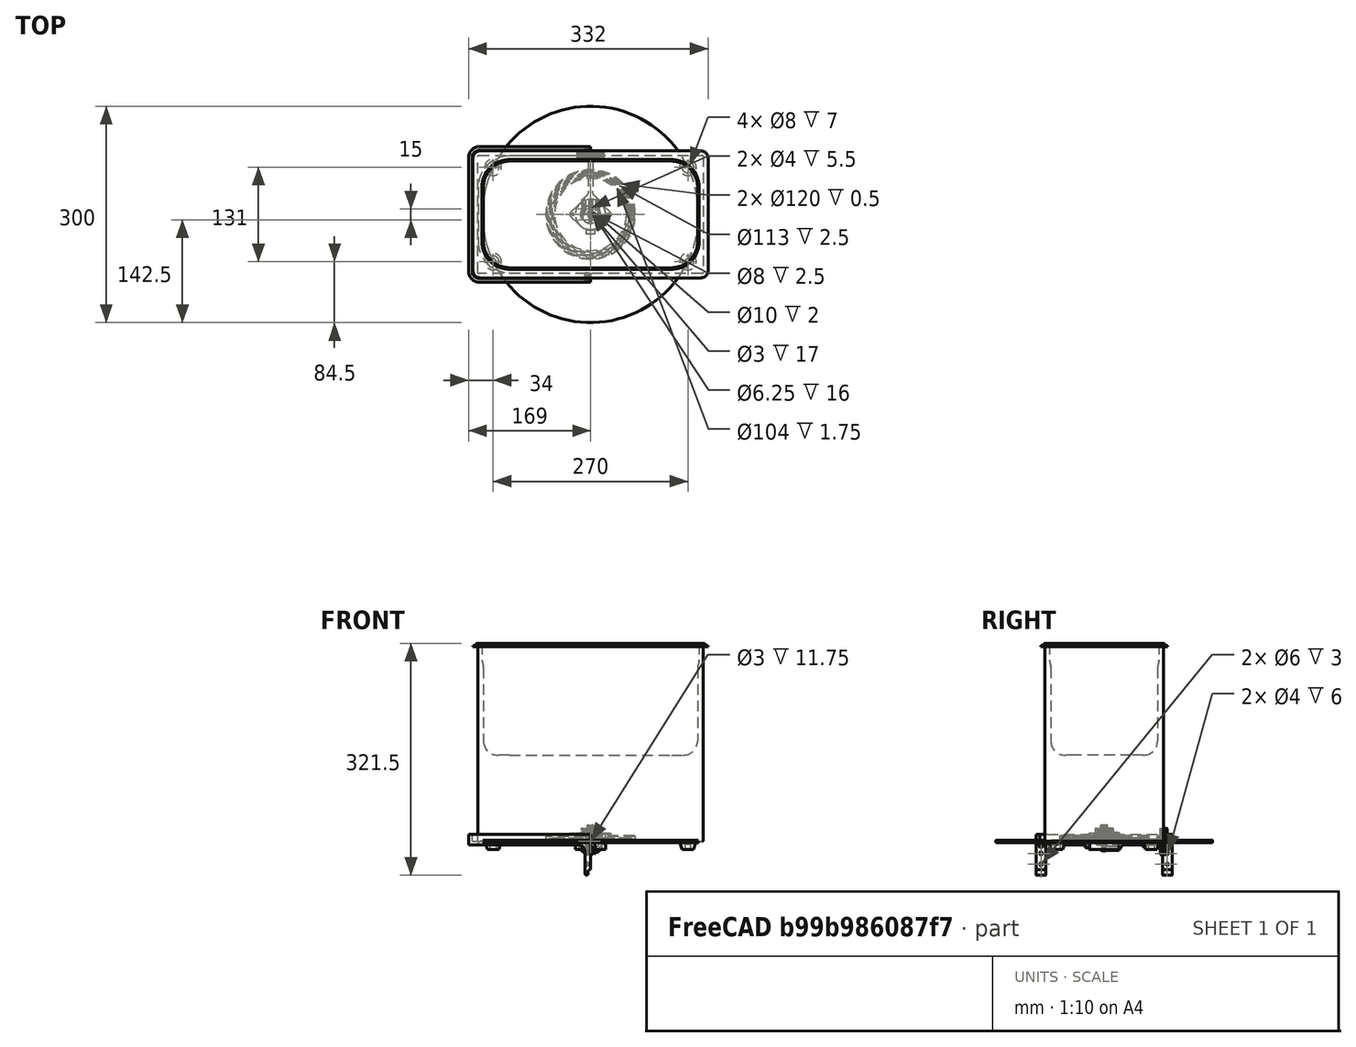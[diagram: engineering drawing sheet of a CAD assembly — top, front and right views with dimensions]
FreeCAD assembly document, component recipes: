
FREECAD ASSEMBLY — COMPONENT RECIPES ("assembly-ultrasonic-cleaner-exploded")

This assembly document has 14 components, labeled P0..P13 below (a component is one placed body or linked part). 14 of them carry a construction recipe — the FreeCAD feature program that regenerates the part from scratch, quoted from this document or its linked companion documents; the rest are supplied as boundary geometry only. No exploded tour is included for this assembly.
NOTE — this tour is split across 2 documents so each fits a 32k-token context. This is document 1: the component sections continue in the remaining 1 document, each repeating the header above.
COMPONENT P0 — recipe-attached ("Body", modeled in this document).
Construction recipe (the document's own serialized feature program — sketch geometry with constraints, then the solid features built on it; lengths are millimeters unless a unit is written):

FEATURE [Sketcher::SketchObject] CopySketch004
  ArcFitTolerance = 0
  ExternalBSplineMaxDegree = 0
  ExternalBSplineTolerance = 0
  FullyConstrained = false
  InternalTolerance = 1e-06
  InvalidShape = false
  MakeInternals = false
  Placement = pos=(0,0,250.5) rot=(0,0,1;0rad)
  TreeRank = 0
  ValidateShape = false
  sketch-geometry (8):
    g0: ArcOfCircle CenterX=112.315 CenterY=-37.8146 CenterZ=0 NormalX=0 NormalY=0 NormalZ=1 AngleXU=0 Radius=38.1854 StartAngle=4.71239 EndAngle=6.28319
    g1: ArcOfCircle CenterX=112.315 CenterY=37.8146 CenterZ=0 NormalX=0 NormalY=0 NormalZ=1 AngleXU=0 Radius=38.1854 StartAngle=2e-16 EndAngle=1.5708
    g2: ArcOfCircle CenterX=-112.315 CenterY=37.8146 CenterZ=0 NormalX=0 NormalY=0 NormalZ=1 AngleXU=0 Radius=38.1854 StartAngle=1.5708 EndAngle=3.14159
    g3: ArcOfCircle CenterX=-112.315 CenterY=-37.8146 CenterZ=0 NormalX=0 NormalY=0 NormalZ=1 AngleXU=0 Radius=38.1854 StartAngle=3.14159 EndAngle=4.71239
    g4: LineSegment StartX=150.5 StartY=-37.8146 StartZ=0 EndX=150.5 EndY=37.8146 EndZ=0
    g5: LineSegment StartX=112.315 StartY=-76 StartZ=0 EndX=-112.315 EndY=-76 EndZ=0
    g6: LineSegment StartX=-150.5 StartY=-37.8146 StartZ=0 EndX=-150.5 EndY=37.8146 EndZ=0
    g7: LineSegment StartX=112.315 StartY=76 StartZ=0 EndX=-112.315 EndY=76 EndZ=0
  constraints (14):
    c: Symmetric(g4,g6,g-2)
    c: Symmetric(g6,g4,g-2)
    c: Symmetric(g4,g4,g-1)
    c: Symmetric(g5,g7,g-1)
    c: Symmetric(g5,g7,g-1)
    c: Symmetric(g5,g5,g-2)
    c: Tangent(g0,g4) = -1.5708
    c: Tangent(g4,g1) = -1.5708
    c: Tangent(g1,g7) = -1.5708
    c: Tangent(g2,g7) = -1.5708
    c: Tangent(g6,g2) = 1.5708
    c: Tangent(g3,g6) = 1.5708
    c: Tangent(g3,g5) = 1.5708
    c: Tangent(g0,g5) = 1.5708
FEATURE [Sketcher::SketchObject] Sketch
  ArcFitTolerance = 0
  AttachmentSupport = -> [XY_Plane]
  ExternalBSplineMaxDegree = 0
  ExternalBSplineTolerance = 0
  FullyConstrained = false
  InternalTolerance = 1e-06
  InvalidShape = false
  MakeInternals = false
  MapMode = 5
  Support = -> [XY_Plane]
  TreeRank = 0
  ValidateShape = false
  sketch-geometry (4):
    g0: LineSegment StartX=-156 StartY=82 StartZ=0 EndX=156 EndY=82 EndZ=0
    g1: LineSegment StartX=156 StartY=82 StartZ=0 EndX=156 EndY=-82 EndZ=0
    g2: LineSegment StartX=156 StartY=-82 StartZ=0 EndX=-156 EndY=-82 EndZ=0
    g3: LineSegment StartX=-156 StartY=-82 StartZ=0 EndX=-156 EndY=82 EndZ=0
  constraints (10):
    c: Coincident(g0,g1)
    c: Coincident(g1,g2)
    c: Coincident(g2,g3)
    c: Coincident(g3,g0)
    c: Horizontal(g2)
    c: Vertical(g1)
    c: Symmetric(g0,g2,g-1)
    c: Symmetric(g0,g0,g-2)
    c: DistanceX(g0,g0) = 312
    c: DistanceY(g3,g3) = 164
FEATURE [PartDesign::Pad] Pad
  AddSubType = 0
  AllowMultiFace = false
  AutoTaperInnerAngle = true
  CheckUpToFaceLimits = true
  ClaimChildren = false
  Direction = (1,1,1)
  Fit = 0
  FitJoin = 0
  InnerFit = 0
  InnerFitJoin = 0
  InvalidShape = false
  Length = 270
  Length2 = 100
  NewSolid = false
  Profile = -> Sketch
  Suppress = false
  TaperInnerAngle = 0
  TaperInnerAngleRev = 0
  TreeRank = 0
  Type = 0
  ValidateShape = true
  _ProfileBasedVersion = 0
FEATURE [Sketcher::SketchObject] Sketch001
  ArcFitTolerance = 0
  AttachmentSupport = -> [Pad]
  ExternalBSplineMaxDegree = 0
  ExternalBSplineTolerance = 0
  FullyConstrained = false
  InternalTolerance = 1e-06
  InvalidShape = false
  MakeInternals = false
  MapMode = 5
  Placement = pos=(0,0,270) rot=(0,0,1;0rad)
  Support = -> [Pad]
  TreeRank = 0
  ValidateShape = false
  sketch-geometry (4):
    g0: LineSegment StartX=-163 StartY=88 StartZ=0 EndX=163 EndY=88 EndZ=0
    g1: LineSegment StartX=163 StartY=88 StartZ=0 EndX=163 EndY=-88 EndZ=0
    g2: LineSegment StartX=163 StartY=-88 StartZ=0 EndX=-163 EndY=-88 EndZ=0
    g3: LineSegment StartX=-163 StartY=-88 StartZ=0 EndX=-163 EndY=88 EndZ=0
  constraints (10):
    c: Coincident(g0,g1)
    c: Coincident(g1,g2)
    c: Coincident(g2,g3)
    c: Coincident(g3,g0)
    c: Horizontal(g2)
    c: Vertical(g1)
    c: DistanceX(g0,g0) = 326
    c: DistanceY(g3,g3) = 176
    c: Symmetric(g0,g2,g-1)
    c: Symmetric(g0,g0,g-2)
FEATURE [PartDesign::Pad] Pad001
  AddSubType = 0
  AllowMultiFace = false
  AutoTaperInnerAngle = true
  BaseFeature = -> Pad
  CheckUpToFaceLimits = true
  ClaimChildren = false
  Direction = (1,1,1)
  Fit = 0
  FitJoin = 0
  InnerFit = 0
  InnerFitJoin = 0
  InvalidShape = false
  Length = 1.5
  Length2 = 100
  NewSolid = false
  Profile = -> Sketch001
  Suppress = false
  TaperInnerAngle = 0
  TaperInnerAngleRev = 0
  TreeRank = 0
  Type = 0
  ValidateShape = true
  _ProfileBasedVersion = 0
FEATURE [PartDesign::Fillet] Fillet
  AddSubType = 0
  Base = -> Pad001 [Edge22,Edge18,Edge17,Edge20]
  BaseFeature = -> Pad001
  InvalidShape = false
  NewSolid = false
  Radius = 10
  SupportTransform = false
  Suppress = false
  TreeRank = 0
  UseAllEdges = false
  ValidateShape = true
FEATURE [Sketcher::SketchObject] Sketch002
  ArcFitTolerance = 0
  AttachmentSupport = -> [Fillet]
  ExternalBSplineMaxDegree = 0
  ExternalBSplineTolerance = 0
  ExternalGeometry = -> [Fillet]
  FullyConstrained = false
  InternalTolerance = 1e-06
  InvalidShape = false
  MakeInternals = false
  MapMode = 5
  Placement = pos=(0,0,271.5) rot=(0,0,1;0rad)
  Support = -> [Fillet]
  TreeRank = 0
  ValidateShape = false
  sketch-geometry (8):
    g0: LineSegment StartX=-158 StartY=78 StartZ=0 EndX=-158 EndY=-78 EndZ=0
    g1: LineSegment StartX=-153 StartY=-83 StartZ=0 EndX=153 EndY=-83 EndZ=0
    g2: LineSegment StartX=158 StartY=-78 StartZ=0 EndX=158 EndY=78 EndZ=0
    g3: LineSegment StartX=153 StartY=83 StartZ=0 EndX=-153 EndY=83 EndZ=0
    g4: ArcOfCircle CenterX=-153 CenterY=78 CenterZ=0 NormalX=0 NormalY=0 NormalZ=1 AngleXU=0 Radius=5 StartAngle=1.5708 EndAngle=3.14159
    g5: ArcOfCircle CenterX=-153 CenterY=-78 CenterZ=0 NormalX=0 NormalY=0 NormalZ=1 AngleXU=0 Radius=5 StartAngle=3.14159 EndAngle=4.71239
    g6: ArcOfCircle CenterX=153 CenterY=-78 CenterZ=0 NormalX=0 NormalY=0 NormalZ=1 AngleXU=0 Radius=5 StartAngle=4.71239 EndAngle=6.28319
    g7: ArcOfCircle CenterX=153 CenterY=78 CenterZ=0 NormalX=0 NormalY=0 NormalZ=1 AngleXU=0 Radius=5 StartAngle=-9e-16 EndAngle=1.5708
  constraints (17):
    c: Vertical(g0)
    c: Horizontal(g1)
    c: Symmetric(g1,g3,g-1)
    c: Symmetric(g3,g1,g-1)
    c: Symmetric(g0,g2,g-2)
    c: Symmetric(g2,g0,g-2)
    c: Tangent(g7,g3) = -1.5708
    c: Tangent(g7,g2) = -1.5708
    c: Tangent(g6,g2) = -1.5708
    c: Tangent(g1,g6) = -1.5708
    c: Tangent(g1,g5) = -1.5708
    c: Tangent(g5,g0) = -1.5708
    c: Tangent(g4,g0) = -1.5708
    c: Tangent(g4,g3) = -1.5708
    c: DistanceY(g3,g-10) = 5
    c: DistanceX(g-4,g0) = 5
    c: Horizontal(g-4,g0)
FEATURE [PartDesign::Pad] Pad002
  AddSubType = 0
  AllowMultiFace = false
  AutoTaperInnerAngle = true
  BaseFeature = -> Fillet
  CheckUpToFaceLimits = true
  ClaimChildren = false
  Direction = (1,1,1)
  Fit = 0
  FitJoin = 0
  InnerFit = 0
  InnerFitJoin = 0
  InvalidShape = false
  Length = 3
  Length2 = 100
  NewSolid = false
  Profile = -> Sketch002
  Suppress = false
  TaperInnerAngle = 0
  TaperInnerAngleRev = 0
  TreeRank = 0
  Type = 0
  ValidateShape = true
  _ProfileBasedVersion = 0
FEATURE [PartDesign::Draft] Draft
  AddSubType = 0
  Angle = 45
  Base = -> Pad002 [Face21,Face22,Face23,Face16,Face17,Face18,Face19,Face20]
  BaseFeature = -> Pad002
  InvalidShape = false
  NeutralPlane = -> Pad002 [Face24]
  NewSolid = false
  SupportTransform = false
  Suppress = false
  TreeRank = 0
  ValidateShape = true
FEATURE [PartDesign::Fillet] Fillet001
  AddSubType = 0
  Base = -> Draft [Edge59,Edge60,Edge44,Edge43,Edge42,Edge57,Edge55,Edge41,Edge53,Edge40,Edge51,Edge49,Edge38,Edge39,Edge47,Edge37]
  BaseFeature = -> Draft
  InvalidShape = false
  NewSolid = false
  Radius = 4
  SupportTransform = false
  Suppress = false
  TreeRank = 0
  UseAllEdges = false
  ValidateShape = true
FEATURE [Sketcher::SketchObject] Sketch003
  ArcFitTolerance = 0
  AttachmentSupport = -> [Fillet001]
  ExternalBSplineMaxDegree = 0
  ExternalBSplineTolerance = 0
  ExternalGeometry = -> [Fillet001]
  FullyConstrained = false
  InternalTolerance = 1e-06
  InvalidShape = false
  MakeInternals = false
  MapMode = 5
  Placement = pos=(0,0,274.5) rot=(0,0,1;0rad)
  Support = -> [Fillet001]
  TreeRank = 0
  ValidateShape = false
  sketch-geometry (9):
    g0: ArcOfCircle CenterX=-112.315 CenterY=37.8146 CenterZ=0 NormalX=0 NormalY=0 NormalZ=1 AngleXU=0 Radius=38.1854 StartAngle=1.5708 EndAngle=3.14159
    g1: ArcOfCircle CenterX=-112.315 CenterY=-37.8146 CenterZ=0 NormalX=0 NormalY=0 NormalZ=1 AngleXU=0 Radius=38.1854 StartAngle=3.14159 EndAngle=4.71239
    g2: ArcOfCircle CenterX=112.315 CenterY=-37.8146 CenterZ=0 NormalX=0 NormalY=0 NormalZ=1 AngleXU=0 Radius=38.1854 StartAngle=4.71239 EndAngle=6.28319
    g3: ArcOfCircle CenterX=112.315 CenterY=37.8146 CenterZ=0 NormalX=0 NormalY=0 NormalZ=1 AngleXU=0 Radius=38.1854 StartAngle=0 EndAngle=1.5708
    g4: LineSegment StartX=-150.5 StartY=37.8146 StartZ=0 EndX=-150.5 EndY=-37.8146 EndZ=0
    g5: LineSegment StartX=-112.315 StartY=76 StartZ=0 EndX=112.315 EndY=76 EndZ=0
    g6: LineSegment StartX=-112.315 StartY=-76 StartZ=0 EndX=112.315 EndY=-76 EndZ=0
    g7: LineSegment StartX=150.5 StartY=-37.8146 StartZ=0 EndX=150.5 EndY=37.8146 EndZ=0
    g8: LineSegment [constr] StartX=160.115 StartY=85.0272 StartZ=0 EndX=139.482 EndY=64.6483 EndZ=0
  constraints (21):
    c: Symmetric(g7,g4,g-2)
    c: Symmetric(g4,g7,g-2)
    c: Symmetric(g4,g4,g-1)
    c: Symmetric(g6,g6,g-2)
    c: Symmetric(g6,g5,g-1)
    c: Symmetric(g5,g6,g-1)
    c: Tangent(g0,g4) = -1.5708
    c: Tangent(g0,g5) = 1.5708
    c: Tangent(g4,g1) = -1.5708
    c: Tangent(g1,g6) = -1.5708
    c: Coincident(g2,g7)
    c: Tangent(g3,g5) = 1.5708
    c: Tangent(g3,g7) = -1.5708
    c: DistanceY(g3,g-5) = 12
    c: DistanceX(g3,g-6) = 12.5
    c: PointOnObject(g8,g-7)
    c: PointOnObject(g8,g3)
    c: Perpendicular(g-7,g8)
    c: Perpendicular(g3,g8)
    c: Distance(g8) = 29
    c: Tangent(g2,g6) = -1.5708
FEATURE [PartDesign::Pocket] Pocket
  AddSubType = 1
  AllowMultiFace = false
  AutoTaperInnerAngle = true
  BaseFeature = -> Fillet001
  CheckUpToFaceLimits = true
  ClaimChildren = false
  Direction = (1,1,1)
  Fit = 0
  FitJoin = 0
  InnerFit = 0
  InnerFitJoin = 0
  InvalidShape = false
  Length = 24
  Length2 = 100
  NewSolid = false
  Profile = -> Sketch003
  Suppress = false
  TaperInnerAngle = 0
  TaperInnerAngleRev = 0
  TreeRank = 0
  Type = 0
  ValidateShape = true
  _ProfileBasedVersion = 0
  _Version = 0
FEATURE [Sketcher::SketchObject] Sketch004
  ArcFitTolerance = 0
  AttachmentSupport = -> [Pocket]
  ExternalBSplineMaxDegree = 0
  ExternalBSplineTolerance = 0
  ExternalGeometry = -> [Pocket]
  FullyConstrained = false
  InternalTolerance = 1e-06
  InvalidShape = false
  MakeInternals = false
  MapMode = 5
  Placement = pos=(0,0,250.5) rot=(0,0,1;0rad)
  Support = -> [Pocket]
  TreeRank = 0
  ValidateShape = false
  sketch-geometry (8):
    g0: ArcOfCircle CenterX=112.315 CenterY=-37.8146 CenterZ=0 NormalX=0 NormalY=0 NormalZ=1 AngleXU=0 Radius=38.1854 StartAngle=4.71239 EndAngle=6.28319
    g1: ArcOfCircle CenterX=112.315 CenterY=37.8146 CenterZ=0 NormalX=0 NormalY=0 NormalZ=1 AngleXU=0 Radius=38.1854 StartAngle=2e-16 EndAngle=1.5708
    g2: ArcOfCircle CenterX=-112.315 CenterY=37.8146 CenterZ=0 NormalX=0 NormalY=0 NormalZ=1 AngleXU=0 Radius=38.1854 StartAngle=1.5708 EndAngle=3.14159
    g3: ArcOfCircle CenterX=-112.315 CenterY=-37.8146 CenterZ=0 NormalX=0 NormalY=0 NormalZ=1 AngleXU=0 Radius=38.1854 StartAngle=3.14159 EndAngle=4.71239
    g4: LineSegment StartX=150.5 StartY=-37.8146 StartZ=0 EndX=150.5 EndY=37.8146 EndZ=0
    g5: LineSegment StartX=112.315 StartY=-76 StartZ=0 EndX=-112.315 EndY=-76 EndZ=0
    g6: LineSegment StartX=-150.5 StartY=-37.8146 StartZ=0 EndX=-150.5 EndY=37.8146 EndZ=0
    g7: LineSegment StartX=112.315 StartY=76 StartZ=0 EndX=-112.315 EndY=76 EndZ=0
  constraints (17):
    c: Symmetric(g4,g6,g-2)
    c: Symmetric(g6,g4,g-2)
    c: Symmetric(g4,g4,g-1)
    c: Symmetric(g5,g7,g-1)
    c: Symmetric(g5,g7,g-1)
    c: Symmetric(g5,g5,g-2)
    c: Tangent(g0,g4) = -1.5708
    c: Tangent(g4,g1) = -1.5708
    c: Tangent(g1,g7) = -1.5708
    c: Tangent(g2,g7) = -1.5708
    c: Tangent(g6,g2) = 1.5708
    c: Tangent(g3,g6) = 1.5708
    c: Tangent(g3,g5) = 1.5708
    c: Tangent(g0,g5) = 1.5708
    c: DistanceY(g-8,g0) = 0
    c: DistanceX(g0,g-7) = 0
    c: Vertical(g0,g-8)
FEATURE [PartDesign::SubtractiveLoft] SubtractiveLoft
  AddSubType = 1
  AllowMultiFace = false
  BaseFeature = -> Pocket
  ClaimChildren = false
  Closed = false
  Fit = 0
  FitJoin = 0
  InnerFit = 0
  InnerFitJoin = 0
  InvalidShape = false
  MaxDegree = 5
  NewSolid = false
  Profile = -> CopySketch004
  Ruled = false
  Sections = -> [Sketch005]
  SplitProfile = false
  Suppress = false
  TreeRank = 0
  ValidateShape = true
  _ProfileBasedVersion = 0
FEATURE [PartDesign::Pocket] Pocket001
  AddSubType = 1
  AllowMultiFace = false
  AutoTaperInnerAngle = true
  BaseFeature = -> SubtractiveLoft
  CheckUpToFaceLimits = true
  ClaimChildren = false
  Direction = (1,1,1)
  Fit = 0
  FitJoin = 0
  InnerFit = 0
  InnerFitJoin = 0
  InvalidShape = false
  Length = 0
  Length2 = 100
  NewSolid = false
  Profile = -> CopySketch005
  Suppress = false
  TaperInnerAngle = 0
  TaperInnerAngleRev = 0
  TreeRank = 0
  Type = 3
  UpToFace = -> Plane001 [Face1]
  ValidateShape = true
  _ProfileBasedVersion = 0
  _Version = 0
FEATURE [PartDesign::Fillet] Fillet002
  AddSubType = 0
  Base = -> Pocket001 [Face50,Face51,Face49,Face56,Face55,Face54,Face53,Face52]
  BaseFeature = -> Pocket001
  InvalidShape = false
  NewSolid = false
  Radius = 10
  SupportTransform = false
  Suppress = false
  TreeRank = 0
  UseAllEdges = false
  ValidateShape = true
FEATURE [PartDesign::Fillet] Fillet003
  AddSubType = 0
  Base = -> Fillet002 [Face58]
  BaseFeature = -> Fillet002
  InvalidShape = false
  NewSolid = false
  Radius = 20
  SupportTransform = false
  Suppress = false
  TreeRank = 0
  UseAllEdges = false
  ValidateShape = true
FEATURE [Sketcher::SketchObject] Sketch006
  ArcFitTolerance = 0
  AttachmentSupport = -> [Fillet003]
  ExternalBSplineMaxDegree = 0
  ExternalBSplineTolerance = 0
  FullyConstrained = false
  InternalTolerance = 1e-06
  InvalidShape = false
  MakeInternals = false
  MapMode = 5
  Placement = pos=(0,0,0) rot=(1,0,0;3.14159rad)
  Support = -> [Fillet003]
  TreeRank = 0
  ValidateShape = false
  sketch-geometry (4):
    g0: Circle [constr] CenterX=-135 CenterY=65.5 CenterZ=0 NormalX=0 NormalY=0 NormalZ=1 AngleXU=0 Radius=11.5
    g1: Circle [constr] CenterX=135 CenterY=65.5 CenterZ=0 NormalX=0 NormalY=0 NormalZ=1 AngleXU=0 Radius=11.5
    g2: Circle CenterX=135 CenterY=-65.5 CenterZ=0 NormalX=0 NormalY=0 NormalZ=1 AngleXU=0 Radius=11.5
    g3: Circle [constr] CenterX=-135 CenterY=-65.5 CenterZ=0 NormalX=0 NormalY=0 NormalZ=1 AngleXU=0 Radius=11.5
  constraints (9):
    c: Symmetric(g0,g1,g-2)
    c: Symmetric(g3,g2,g-2)
    c: Symmetric(g3,g0,g-1)
    c: Equal(g0,g1)
    c: Equal(g1,g2)
    c: Equal(g2,g3)
    c: Diameter(g1) = 23
    c: DistanceY(g2,g1) = 131
    c: DistanceX(g3,g2) = 270
FEATURE [PartDesign::AdditiveLoft] AdditiveLoft
  AddSubType = 0
  AllowMultiFace = false
  BaseFeature = -> Fillet003
  ClaimChildren = false
  Closed = false
  Fit = 0
  FitJoin = 0
  InnerFit = 0
  InnerFitJoin = 0
  InvalidShape = false
  MaxDegree = 5
  NewSolid = false
  Profile = -> Sketch006
  Ruled = false
  Sections = -> [Sketch007]
  SplitProfile = false
  Suppress = false
  TreeRank = 0
  ValidateShape = true
  _ProfileBasedVersion = 0
FEATURE [Sketcher::SketchObject] Sketch008
  ArcFitTolerance = 0
  AttachmentSupport = -> [AdditiveLoft]
  ExternalBSplineMaxDegree = 0
  ExternalBSplineTolerance = 0
  ExternalGeometry = -> [AdditiveLoft]
  FullyConstrained = false
  InternalTolerance = 1e-06
  InvalidShape = false
  MakeInternals = false
  MapMode = 5
  Placement = pos=(-8e-16,-1.4e-15,-11) rot=(1,0,0;3.14159rad)
  Support = -> [AdditiveLoft]
  TreeRank = 0
  ValidateShape = false
  sketch-geometry (1):
    g0: Circle CenterX=135 CenterY=-65.5 CenterZ=0 NormalX=0 NormalY=0 NormalZ=1 AngleXU=0 Radius=4
  constraints (2):
    c: Coincident(g0,g-3)
    c: Diameter(g0) = 8
FEATURE [PartDesign::Pocket] Pocket002
  AddSubType = 1
  AllowMultiFace = false
  AutoTaperInnerAngle = true
  BaseFeature = -> AdditiveLoft
  CheckUpToFaceLimits = true
  ClaimChildren = false
  Direction = (1,1,1)
  Fit = 0
  FitJoin = 0
  InnerFit = 0
  InnerFitJoin = 0
  InvalidShape = false
  Length = 7
  Length2 = 100
  NewSolid = false
  Profile = -> Sketch008
  Suppress = false
  TaperInnerAngle = 0
  TaperInnerAngleRev = 0
  TreeRank = 0
  Type = 0
  ValidateShape = true
  _ProfileBasedVersion = 0
  _Version = 0
FEATURE [PartDesign::Mirrored] Mirrored001
  AddSubType = 0
  CopyShape = true
  InvalidShape = false
  MirrorPlane = -> Sketch006 [H_Axis]
  NewSolid = false
  ParallelTransform = true
  SubTransform = true
  Suppress = false
  TreeRank = 0
  ValidateShape = true
  _Version = 0
FEATURE [PartDesign::Mirrored] Mirrored
  AddSubType = 0
  CopyShape = true
  InvalidShape = false
  MirrorPlane = -> Sketch006 [V_Axis]
  NewSolid = false
  ParallelTransform = true
  SubTransform = true
  Suppress = false
  TreeRank = 0
  ValidateShape = true
  _Version = 0
FEATURE [PartDesign::MultiTransform] MultiTransform
  AddSubType = 0
  BaseFeature = -> Pocket002
  CopyShape = true
  InvalidShape = false
  NewSolid = false
  OriginalSubs = -> [AdditiveLoft,Pocket002]
  Originals = -> [AdditiveLoft,Pocket002]
  ParallelTransform = true
  SubTransform = true
  Suppress = false
  Transformations = -> [Mirrored,Mirrored001]
  TreeRank = 0
  ValidateShape = true
  _Version = 0
FEATURE [PartDesign::Fillet] Fillet004
  AddSubType = 0
  Base = -> MultiTransform [Edge190,Edge189,Edge191,Edge193,Edge195,Edge196,Edge194,Edge192]
  BaseFeature = -> MultiTransform
  InvalidShape = false
  NewSolid = false
  Radius = 1
  SupportTransform = false
  Suppress = false
  TreeRank = 0
  UseAllEdges = false
  ValidateShape = true
FEATURE [PartDesign::Fillet] Fillet005
  AddSubType = 0
  Base = -> Fillet004 [Edge1,Edge3,Edge5,Edge7,Edge8,Edge6,Edge4,Edge2]
  BaseFeature = -> Fillet004
  InvalidShape = false
  NewSolid = false
  Radius = 3
  SupportTransform = false
  Suppress = false
  TreeRank = 0
  UseAllEdges = false
  ValidateShape = true
FEATURE [PartDesign::Body] Body
  AutoGroupSolids = false
  ClaimAllChildren = false
  ExportMode = 0
  Group = -> [Sketch,Pad,Sketch001,Pad001,Fillet,Sketch002,Pad002,Draft,Fillet001,Sketch003,Pocket,Sketch004,CopySketch004,SubtractiveLoft,Pocket001,Fillet002,Fillet003,Sketch006,AdditiveLoft,Sketch008,Pocket002,MultiTransform,Mirrored,Mirrored001,Fillet004,Fillet005]
  InvalidShape = false
  Origin = -> Origin
  SingleSolid = true
  Tip = -> Fillet005
  TreeRank = 0
  ValidateShape = false
  _ExportChildren = -> [Pad,Pad001,Fillet,Pad002,Draft,Fillet001,Pocket,Sketch004,SubtractiveLoft,Pocket001,Fillet002,Fillet003,AdditiveLoft,Pocket002,MultiTransform,Fillet004,Fillet005]
  _GroupVersion = 1
COMPONENT P1 — recipe-attached ("Body001", modeled in this document).
Construction recipe (the document's own serialized feature program — sketch geometry with constraints, then the solid features built on it; lengths are millimeters unless a unit is written):

FEATURE [Sketcher::SketchObject] Sketch018
  ArcFitTolerance = 0
  AttachmentSupport = -> [XY_Plane001]
  ExternalBSplineMaxDegree = 0
  ExternalBSplineTolerance = 0
  FullyConstrained = false
  InternalTolerance = 1e-06
  InvalidShape = false
  MakeInternals = false
  MapMode = 5
  Support = -> [XY_Plane001]
  TreeRank = 0
  ValidateShape = false
  sketch-geometry (16):
    g0: LineSegment StartX=-154 StartY=89 StartZ=0 EndX=154 EndY=89 EndZ=0
    g1: LineSegment StartX=164 StartY=79 StartZ=0 EndX=164 EndY=-79 EndZ=0
    g2: LineSegment StartX=154 StartY=-89 StartZ=0 EndX=-154 EndY=-89 EndZ=0
    g3: LineSegment StartX=-164 StartY=-79 StartZ=0 EndX=-164 EndY=79 EndZ=0
    g4: ArcOfCircle CenterX=-154 CenterY=79 CenterZ=0 NormalX=0 NormalY=0 NormalZ=1 AngleXU=0 Radius=10 StartAngle=1.5708 EndAngle=3.14159
    g5: ArcOfCircle CenterX=154 CenterY=79 CenterZ=0 NormalX=0 NormalY=0 NormalZ=1 AngleXU=0 Radius=10 StartAngle=-9e-16 EndAngle=1.5708
    g6: ArcOfCircle CenterX=154 CenterY=-79 CenterZ=0 NormalX=0 NormalY=0 NormalZ=1 AngleXU=0 Radius=10 StartAngle=4.71239 EndAngle=6.28319
    g7: ArcOfCircle CenterX=-154 CenterY=-79 CenterZ=0 NormalX=0 NormalY=0 NormalZ=1 AngleXU=0 Radius=10 StartAngle=3.14159 EndAngle=4.71239
    g8: LineSegment StartX=-154 StartY=94 StartZ=0 EndX=154 EndY=94 EndZ=0
    g9: LineSegment StartX=169 StartY=79 StartZ=0 EndX=169 EndY=-79 EndZ=0
    g10: LineSegment StartX=154 StartY=-94 StartZ=0 EndX=-154 EndY=-94 EndZ=0
    g11: LineSegment StartX=-169 StartY=-79 StartZ=0 EndX=-169 EndY=79 EndZ=0
    g12: ArcOfCircle CenterX=-154 CenterY=79 CenterZ=0 NormalX=0 NormalY=0 NormalZ=1 AngleXU=0 Radius=15 StartAngle=1.5708 EndAngle=3.14159
    g13: ArcOfCircle CenterX=154 CenterY=79 CenterZ=0 NormalX=0 NormalY=0 NormalZ=1 AngleXU=0 Radius=15 StartAngle=1e-16 EndAngle=1.5708
    g14: ArcOfCircle CenterX=154 CenterY=-79 CenterZ=0 NormalX=0 NormalY=0 NormalZ=1 AngleXU=0 Radius=15 StartAngle=4.71239 EndAngle=6.28319
    g15: ArcOfCircle CenterX=-154 CenterY=-79 CenterZ=0 NormalX=0 NormalY=0 NormalZ=1 AngleXU=0 Radius=15 StartAngle=3.14159 EndAngle=4.71239
  constraints (35):
    c: Tangent(g3,g4) = 1.5708
    c: Tangent(g0,g4) = 1.5708
    c: Tangent(g0,g5) = 1.5708
    c: Tangent(g1,g5) = 1.5708
    c: Tangent(g1,g6) = 1.5708
    c: Tangent(g2,g6) = 1.5708
    c: Tangent(g2,g7) = 1.5708
    c: Tangent(g3,g7) = 1.5708
    c: Equal(g5,g6)
    c: Equal(g6,g7)
    c: Equal(g7,g4)
    c: Symmetric(g3,g1,g-2)
    c: Symmetric(g3,g1,g-2)
    c: Symmetric(g3,g3,g-1)
    c: DistanceX(g3,g1) = 328
    c: DistanceY(g2,g0) = 178
    c: Radius(g5) = 10
    c: Tangent(g11,g12) = 1.5708
    c: Tangent(g8,g12) = 1.5708
    c: Tangent(g8,g13) = 1.5708
    c: Tangent(g9,g13) = 1.5708
    c: Tangent(g9,g14) = 1.5708
    c: Tangent(g10,g14) = 1.5708
    c: Tangent(g10,g15) = 1.5708
    c: Tangent(g11,g15) = 1.5708
    c: Horizontal(g8)
    c: Horizontal(g10)
    c: Vertical(g9)
    c: Vertical(g11)
    c: DistanceX(g11,g3) = 5
    c: DistanceY(g0,g8) = 5
    c: Equal(g14,g13)
    c: Equal(g13,g12)
    c: Coincident(g15,g7)
    c: Coincident(g13,g5)
FEATURE [PartDesign::Pad] Pad007
  AddSubType = 0
  AutoTaperInnerAngle = true
  CheckUpToFaceLimits = true
  ClaimChildren = false
  Direction = (1,1,1)
  Fit = 0
  FitJoin = 0
  InnerFit = 0
  InnerFitJoin = 0
  InvalidShape = false
  Length = 10
  Length2 = 100
  NewSolid = false
  Profile = -> Sketch018
  Suppress = false
  TaperInnerAngle = 0
  TaperInnerAngleRev = 0
  TreeRank = 0
  Type = 0
  ValidateShape = true
  _ProfileBasedVersion = 0
FEATURE [PartDesign::Pad] Pad006
  AddSubType = 0
  AutoTaperInnerAngle = true
  BaseFeature = -> Pad007
  CheckUpToFaceLimits = true
  ClaimChildren = false
  Direction = (0,0,1)
  Fit = 0
  FitJoin = 0
  InnerFit = 0
  InnerFitJoin = 0
  InvalidShape = false
  Length = 5
  Length2 = 100
  NewSolid = false
  Profile = -> Sketch019
  Reversed = true
  Suppress = false
  TaperInnerAngle = 0
  TaperInnerAngleRev = 0
  TreeRank = 0
  Type = 0
  ValidateShape = true
  _ProfileBasedVersion = 0
FEATURE [Sketcher::SketchObject] Sketch017
  ArcFitTolerance = 0
  AttachmentSupport = -> [Pad006]
  ExternalBSplineMaxDegree = 0
  ExternalBSplineTolerance = 0
  ExternalGeometry = -> [Pad006]
  FullyConstrained = true
  InternalTolerance = 1e-06
  InvalidShape = false
  MakeInternals = false
  MapMode = 5
  Placement = pos=(0,94,0) rot=(0,0.707107,0.707107;3.14159rad)
  Support = -> [Pad006]
  TreeRank = 0
  ValidateShape = false
  sketch-geometry (6):
    g0: LineSegment StartX=-7.36667 StartY=-5 StartZ=0 EndX=7.36667 EndY=-5 EndZ=0
    g1: LineSegment StartX=-7.36667 StartY=-5 StartZ=0 EndX=-7.36667 EndY=-45 EndZ=0
    g2: LineSegment StartX=7.36667 StartY=-45 StartZ=0 EndX=7.36667 EndY=-5 EndZ=0
    g3: ArcOfCircle CenterX=5.36667 CenterY=-45 CenterZ=0 NormalX=0 NormalY=0 NormalZ=1 AngleXU=0 Radius=2 StartAngle=2.77438 EndAngle=6.28319
    g4: ArcOfCircle CenterX=-1e-16 CenterY=-42.9357 CenterZ=0 NormalX=0 NormalY=0 NormalZ=1 AngleXU=0 Radius=3.75 StartAngle=5.91598 EndAngle=9.79199
    g5: ArcOfCircle CenterX=-5.36667 CenterY=-45 CenterZ=0 NormalX=0 NormalY=0 NormalZ=1 AngleXU=0 Radius=2 StartAngle=3.14159 EndAngle=6.65039
  constraints (15):
    c: Symmetric(g0,g0,g-2)
    c: Coincident(g1,g0)
    c: Vertical(g1)
    c: Coincident(g2,g0)
    c: PointOnObject(g0,g-4)
    c: Symmetric(g2,g1,g-2)
    c: Tangent(g3,g2) = -1.5708
    c: Coincident(g5,g4)
    c: Tangent(g1,g5) = -1.5708
    c: Symmetric(g3,g4,g-2)
    c: Tangent(g4,g3) = 1.5708
    c: Diameter(g4) = 7.5
    c: Radius(g3) = 2
    c: DistanceX(g4,g3) = 7
    c: DistanceY(g1,g1) = 40
FEATURE [PartDesign::Pad] Pad005
  AddSubType = 0
  AutoTaperInnerAngle = true
  BaseFeature = -> Pad006
  CheckUpToFaceLimits = true
  ClaimChildren = false
  Direction = (0,1,-2e-16)
  Fit = 0
  FitJoin = 0
  InnerFit = 0
  InnerFitJoin = 0
  InvalidShape = false
  Length = 10
  Length2 = 100
  NewSolid = false
  Profile = -> Sketch017
  Reversed = true
  Suppress = false
  TaperInnerAngle = 0
  TaperInnerAngleRev = 0
  TreeRank = 0
  Type = 3
  UpToFace = -> Pad006 [Face27]
  ValidateShape = true
  _ProfileBasedVersion = 0
FEATURE [PartDesign::Mirrored] Mirrored003
  AddSubType = 0
  BaseFeature = -> Pad005
  CopyShape = true
  InvalidShape = false
  MirrorPlane = -> XZ_Plane001
  NewSolid = false
  OriginalSubs = -> [Pad005]
  Originals = -> [Pad005]
  ParallelTransform = true
  SubTransform = true
  Suppress = false
  TreeRank = 0
  ValidateShape = true
  _Version = 0
FEATURE [PartDesign::Fillet] Fillet006
  AddSubType = 0
  Base = -> Mirrored003 [Edge104,Edge36,Edge42,Edge100]
  BaseFeature = -> Mirrored003
  InvalidShape = false
  NewSolid = false
  Radius = 10
  SupportTransform = true
  Suppress = false
  TreeRank = 0
  UseAllEdges = false
  ValidateShape = true
FEATURE [Sketcher::SketchObject] Sketch016
  ArcFitTolerance = 0
  AttachmentSupport = -> [Fillet006]
  ExternalBSplineMaxDegree = 0
  ExternalBSplineTolerance = 0
  ExternalGeometry = -> [Fillet006]
  FullyConstrained = true
  InternalTolerance = 1e-06
  InvalidShape = false
  MakeInternals = false
  MapMode = 5
  Placement = pos=(0,94,-3.37e-14) rot=(0,0.707107,0.707107;3.14159rad)
  Support = -> [Fillet006]
  TreeRank = 0
  ValidateShape = false
  sketch-geometry (4):
    g0: LineSegment StartX=-5.36666 StartY=-47 StartZ=0 EndX=5.36667 EndY=-47 EndZ=0
    g1: ArcOfCircle CenterX=-5.36667 CenterY=-45 CenterZ=0 NormalX=0 NormalY=0 NormalZ=1 AngleXU=0 Radius=2 StartAngle=4.71239 EndAngle=6.65039
    g2: ArcOfCircle CenterX=5.36667 CenterY=-45 CenterZ=0 NormalX=0 NormalY=0 NormalZ=1 AngleXU=0 Radius=2 StartAngle=2.77438 EndAngle=4.71239
    g3: ArcOfCircle CenterX=7e-16 CenterY=-42.9357 CenterZ=0 NormalX=0 NormalY=0 NormalZ=1 AngleXU=0 Radius=3.75 StartAngle=5.91598 EndAngle=9.79199
  constraints (11):
    c: Tangent(g0,g-3)
    c: Coincident(g1,g0)
    c: Coincident(g1,g-3)
    c: Coincident(g1,g-4)
    c: Coincident(g2,g0)
    c: Coincident(g2,g-5)
    c: Coincident(g2,g-5)
    c: Tangent(g0,g-5)
    c: Coincident(g3,g2)
    c: Coincident(g3,g1)
    c: Coincident(g3,g-4)
FEATURE [PartDesign::Pad] Pad003
  AddSubType = 0
  AutoTaperInnerAngle = true
  BaseFeature = -> Fillet006
  CheckUpToFaceLimits = true
  ClaimChildren = false
  Direction = (0,1,-4e-16)
  Fit = 0
  FitJoin = 0
  InnerFit = 0
  InnerFitJoin = 0
  InvalidShape = false
  Length = 1.5
  Length2 = 100
  NewSolid = false
  Profile = -> Sketch016
  Reversed = true
  Suppress = false
  TaperInnerAngle = 0
  TaperInnerAngleRev = 0
  TreeRank = 0
  Type = 0
  ValidateShape = true
  _ProfileBasedVersion = 0
FEATURE [PartDesign::Mirrored] Mirrored002
  AddSubType = 0
  BaseFeature = -> Pad003
  CopyShape = true
  InvalidShape = false
  MirrorPlane = -> XZ_Plane001
  NewSolid = false
  OriginalSubs = -> [Pad003]
  Originals = -> [Pad003]
  ParallelTransform = true
  SubTransform = true
  Suppress = false
  TreeRank = 0
  ValidateShape = true
  _Version = 0
FEATURE [PartDesign::Chamfer] Chamfer002
  AddSubType = 0
  Angle = 45
  Base = -> Mirrored002 [Edge114]
  BaseFeature = -> Mirrored002
  ChamferType = 0
  FlipDirection = false
  InvalidShape = false
  NewSolid = false
  Size = 0.1
  Size2 = 1
  SupportTransform = true
  Suppress = false
  TreeRank = 0
  UseAllEdges = false
  ValidateShape = true
FEATURE [Sketcher::SketchObject] Sketch015
  ArcFitTolerance = 0
  AttachmentSupport = -> [Chamfer002]
  ExternalBSplineMaxDegree = 0
  ExternalBSplineTolerance = 0
  FullyConstrained = false
  InternalTolerance = 1e-06
  InvalidShape = false
  MakeInternals = false
  MapMode = 5
  Placement = pos=(0,0,10) rot=(0,0,1;0rad)
  Support = -> [Chamfer002]
  TreeRank = 0
  ValidateShape = false
  sketch-geometry (4):
    g0: LineSegment StartX=0 StartY=119.45 StartZ=0 EndX=0 EndY=-119.45 EndZ=0
    g1: LineSegment StartX=0 StartY=119.45 StartZ=0 EndX=200.233 EndY=119.45 EndZ=0
    g2: LineSegment StartX=200.233 StartY=119.45 StartZ=0 EndX=200.233 EndY=-119.45 EndZ=0
    g3: LineSegment StartX=200.233 StartY=-119.45 StartZ=0 EndX=0 EndY=-119.45 EndZ=0
  constraints (9):
    c: PointOnObject(g0,g-2)
    c: Symmetric(g0,g0,g-1)
    c: Coincident(g0,g1)
    c: Horizontal(g1)
    c: Coincident(g1,g2)
    c: Vertical(g2)
    c: Coincident(g2,g3)
    c: Coincident(g3,g0)
    c: Horizontal(g3)
FEATURE [PartDesign::Pocket] Pocket010
  AddSubType = 1
  AutoTaperInnerAngle = true
  BaseFeature = -> Chamfer002
  CheckUpToFaceLimits = true
  ClaimChildren = false
  Direction = (0,0,-1)
  Fit = 0
  FitJoin = 0
  InnerFit = 0
  InnerFitJoin = 0
  InvalidShape = false
  Length = 5
  Length2 = 100
  NewSolid = false
  Profile = -> Sketch015
  Suppress = false
  TaperInnerAngle = 0
  TaperInnerAngleRev = 0
  TreeRank = 0
  Type = 1
  ValidateShape = true
  _ProfileBasedVersion = 0
  _Version = 0
FEATURE [Sketcher::SketchObject] Sketch014
  ArcFitTolerance = 0
  AttachmentSupport = -> [Pocket010]
  ExternalBSplineMaxDegree = 0
  ExternalBSplineTolerance = 0
  FullyConstrained = true
  InternalTolerance = 1e-06
  InvalidShape = false
  MakeInternals = false
  MapMode = 5
  Placement = pos=(0,0,0) rot=(0.57735,0.57735,0.57735;2.0944rad)
  Support = -> [Pocket010]
  TreeRank = 0
  ValidateShape = false
  sketch-geometry (1):
    g0: Circle CenterX=87.5 CenterY=-5 CenterZ=0 NormalX=0 NormalY=0 NormalZ=1 AngleXU=0 Radius=2
  constraints (3):
    c: Diameter(g0) = 4
    c: DistanceY(g0,g-1) = 5
    c: DistanceX(g-1,g0) = 87.5
FEATURE [PartDesign::Pad] Pad004
  AddSubType = 0
  AutoTaperInnerAngle = true
  BaseFeature = -> Pocket010
  CheckUpToFaceLimits = true
  ClaimChildren = false
  Direction = (1,0,0)
  Fit = 0
  FitJoin = 0
  InnerFit = 0
  InnerFitJoin = 0
  InvalidShape = false
  Length = 5
  Length2 = 100
  NewSolid = false
  Profile = -> Sketch014
  Suppress = false
  TaperInnerAngle = 0
  TaperInnerAngleRev = 0
  TreeRank = 0
  Type = 0
  ValidateShape = true
  _ProfileBasedVersion = 0
FEATURE [Sketcher::SketchObject] Sketch013
  ArcFitTolerance = 0
  AttachmentSupport = -> [Pad004]
  ExternalBSplineMaxDegree = 0
  ExternalBSplineTolerance = 0
  FullyConstrained = true
  InternalTolerance = 1e-06
  InvalidShape = false
  MakeInternals = false
  MapMode = 5
  Placement = pos=(0,0,0) rot=(0.57735,0.57735,0.57735;2.0944rad)
  Support = -> [Pad004]
  TreeRank = 0
  ValidateShape = false
  sketch-geometry (1):
    g0: Circle CenterX=-87.5 CenterY=-5 CenterZ=0 NormalX=0 NormalY=0 NormalZ=1 AngleXU=0 Radius=2.5
  constraints (3):
    c: Diameter(g0) = 5
    c: DistanceY(g0,g-1) = 5
    c: DistanceX(g0,g-1) = 87.5
FEATURE [PartDesign::Pocket] Pocket009
  AddSubType = 1
  AutoTaperInnerAngle = true
  BaseFeature = -> Pad004
  CheckUpToFaceLimits = true
  ClaimChildren = false
  Direction = (-1,0,0)
  Fit = 0
  FitJoin = 0
  InnerFit = 0
  InnerFitJoin = 0
  InvalidShape = false
  Length = 5.5
  Length2 = 100
  NewSolid = false
  Profile = -> Sketch013
  Suppress = false
  TaperInnerAngle = 0
  TaperInnerAngleRev = 0
  TreeRank = 0
  Type = 0
  ValidateShape = true
  _ProfileBasedVersion = 0
  _Version = 0
FEATURE [PartDesign::Chamfer] Chamfer003
  AddSubType = 0
  Angle = 45
  Base = -> Pocket009 [Edge84,Edge115]
  BaseFeature = -> Pocket009
  ChamferType = 0
  FlipDirection = false
  InvalidShape = false
  NewSolid = false
  Size = 1
  Size2 = 1
  SupportTransform = true
  Suppress = false
  TreeRank = 0
  UseAllEdges = false
  ValidateShape = true
FEATURE [Sketcher::SketchObject] Sketch012
  ArcFitTolerance = 0
  AttachmentSupport = -> [Chamfer003]
  ExternalBSplineMaxDegree = 0
  ExternalBSplineTolerance = 0
  FullyConstrained = true
  InternalTolerance = 1e-06
  InvalidShape = false
  MakeInternals = false
  MapMode = 5
  Placement = pos=(0,0,0) rot=(0.57735,0.57735,0.57735;2.0944rad)
  Support = -> [Chamfer003]
  TreeRank = 0
  ValidateShape = false
  sketch-geometry (4):
    g0: Circle CenterX=87.5 CenterY=-16.69 CenterZ=0 NormalX=0 NormalY=0 NormalZ=1 AngleXU=0 Radius=1.65
    g1: Circle CenterX=87.5 CenterY=-31.69 CenterZ=0 NormalX=0 NormalY=0 NormalZ=1 AngleXU=0 Radius=1.65
    g2: Circle CenterX=-87.5 CenterY=-16.69 CenterZ=0 NormalX=0 NormalY=0 NormalZ=1 AngleXU=0 Radius=1.65
    g3: Circle CenterX=-87.5 CenterY=-31.69 CenterZ=0 NormalX=0 NormalY=0 NormalZ=1 AngleXU=0 Radius=1.65
  constraints (10):
    c: Equal(g1,g0)
    c: Equal(g2,g3)
    c: Equal(g3,g0)
    c: Symmetric(g2,g0,g-2)
    c: Symmetric(g3,g1,g-2)
    c: Diameter(g0) = 3.3
    c: DistanceY(g0,g-1) = 16.69
    c: DistanceY(g1,g-1) = 31.69
    c: DistanceX(g-1,g0) = 87.5
    c: DistanceX(g-1,g1) = 87.5
FEATURE [PartDesign::Pocket] Pocket008
  AddSubType = 1
  AutoTaperInnerAngle = true
  BaseFeature = -> Chamfer003
  CheckUpToFaceLimits = true
  ClaimChildren = false
  Direction = (-1,0,0)
  Fit = 0
  FitJoin = 0
  InnerFit = 0
  InnerFitJoin = 0
  InvalidShape = false
  Length = 5
  Length2 = 100
  NewSolid = false
  Profile = -> Sketch012
  Suppress = false
  TaperInnerAngle = 0
  TaperInnerAngleRev = 0
  TreeRank = 0
  Type = 1
  ValidateShape = true
  _ProfileBasedVersion = 0
  _Version = 0
FEATURE [Sketcher::SketchObject] Sketch011
  ArcFitTolerance = 0
  AttachmentSupport = -> [Pocket008]
  ExternalBSplineMaxDegree = 0
  ExternalBSplineTolerance = 0
  FullyConstrained = true
  InternalTolerance = 1e-06
  InvalidShape = false
  MakeInternals = false
  MapMode = 5
  Placement = pos=(-7.36667,0,0) rot=(0.57735,-0.57735,-0.57735;2.0944rad)
  Support = -> [Pocket008]
  TreeRank = 0
  ValidateShape = false
  sketch-geometry (2):
    g0: Circle CenterX=-87.5 CenterY=-16.75 CenterZ=0 NormalX=0 NormalY=0 NormalZ=1 AngleXU=0 Radius=2
    g1: Circle CenterX=-87.5 CenterY=-31.75 CenterZ=0 NormalX=0 NormalY=0 NormalZ=1 AngleXU=0 Radius=2
  constraints (6):
    c: Equal(g1,g0)
    c: Diameter(g0) = 4
    c: DistanceY(g0,g-1) = 16.75
    c: DistanceX(g0,g-1) = 87.5
    c: Vertical(g1,g0)
    c: DistanceY(g1,g0) = 15
FEATURE [PartDesign::Pocket] Pocket003
  AddSubType = 1
  AutoTaperInnerAngle = true
  BaseFeature = -> Pocket008
  CheckUpToFaceLimits = true
  ClaimChildren = false
  Direction = (1,0,0)
  Fit = 0
  FitJoin = 0
  InnerFit = 0
  InnerFitJoin = 0
  InvalidShape = false
  Length = 6
  Length2 = 100
  NewSolid = false
  Profile = -> Sketch011
  Suppress = false
  TaperInnerAngle = 0
  TaperInnerAngleRev = 0
  TreeRank = 0
  Type = 0
  ValidateShape = true
  _ProfileBasedVersion = 0
  _Version = 0
FEATURE [PartDesign::Pocket] Pocket004
  AddSubType = 1
  AutoTaperInnerAngle = true
  BaseFeature = -> Pocket003
  CheckUpToFaceLimits = true
  ClaimChildren = false
  Direction = (1,0,0)
  Fit = 0
  FitJoin = 0
  InnerFit = 0
  InnerFitJoin = 0
  InvalidShape = false
  Length = 5
  Length2 = 100
  NewSolid = false
  Profile = -> Sketch011
  Reversed = true
  Suppress = false
  TaperInnerAngle = 0
  TaperInnerAngleRev = 0
  TreeRank = 0
  Type = 1
  ValidateShape = true
  _ProfileBasedVersion = 0
  _Version = 0
FEATURE [Sketcher::SketchObject] Sketch009
  ArcFitTolerance = 0
  AttachmentSupport = -> [Pocket004]
  ExternalBSplineMaxDegree = 0
  ExternalBSplineTolerance = 0
  FullyConstrained = true
  InternalTolerance = 1e-06
  InvalidShape = false
  MakeInternals = false
  MapMode = 5
  Placement = pos=(-7.36667,0,0) rot=(0.57735,-0.57735,-0.57735;2.0944rad)
  Support = -> [Pocket004]
  TreeRank = 0
  ValidateShape = false
  sketch-geometry (2):
    g0: Circle CenterX=87.5 CenterY=-16.69 CenterZ=0 NormalX=0 NormalY=0 NormalZ=1 AngleXU=0 Radius=3
    g1: Circle CenterX=87.5 CenterY=-31.69 CenterZ=0 NormalX=0 NormalY=0 NormalZ=1 AngleXU=0 Radius=3
  constraints (6):
    c: Equal(g0,g1)
    c: Diameter(g0) = 6
    c: DistanceX(g-1,g0) = 87.5
    c: DistanceY(g0,g-1) = 16.69
    c: DistanceY(g1,g-1) = 31.69
    c: Vertical(g1,g0)
FEATURE [PartDesign::Pocket] Pocket005
  AddSubType = 1
  AutoTaperInnerAngle = true
  BaseFeature = -> Pocket004
  CheckUpToFaceLimits = true
  ClaimChildren = false
  Direction = (1,0,0)
  Fit = 0
  FitJoin = 0
  InnerFit = 0
  InnerFitJoin = 0
  InvalidShape = false
  Length = 3
  Length2 = 100
  NewSolid = false
  Profile = -> Sketch009
  Suppress = false
  TaperInnerAngle = 0
  TaperInnerAngleRev = 0
  TreeRank = 0
  Type = 0
  ValidateShape = true
  _ProfileBasedVersion = 0
  _Version = 0
FEATURE [PartDesign::Pocket] Pocket006
  AddSubType = 1
  AutoTaperInnerAngle = true
  BaseFeature = -> Pocket005
  CheckUpToFaceLimits = true
  ClaimChildren = false
  Direction = (1,0,0)
  Fit = 0
  FitJoin = 0
  InnerFit = 0
  InnerFitJoin = 0
  InvalidShape = false
  Length = 5
  Length2 = 100
  NewSolid = false
  Profile = -> Sketch009
  Reversed = true
  Suppress = false
  TaperInnerAngle = 0
  TaperInnerAngleRev = 0
  TreeRank = 0
  Type = 1
  ValidateShape = true
  _ProfileBasedVersion = 0
  _Version = 0
FEATURE [PartDesign::Pocket] Pocket007
  AddSubType = 1
  AutoTaperInnerAngle = true
  BaseFeature = -> Pocket006
  CheckUpToFaceLimits = true
  ClaimChildren = false
  Direction = (0,1,0)
  Fit = 0
  FitJoin = 0
  InnerFit = 0
  InnerFitJoin = 0
  InvalidShape = false
  Length = 5
  Length2 = 100
  Midplane = true
  NewSolid = false
  Profile = -> Pocket006 [Face17]
  Suppress = false
  TaperInnerAngle = 0
  TaperInnerAngleRev = 0
  TreeRank = 0
  Type = 1
  ValidateShape = true
  _ProfileBasedVersion = 0
  _Version = 0
FEATURE [Sketcher::SketchObject] Sketch010
  ArcFitTolerance = 0
  AttachmentSupport = -> [Pocket007]
  ExternalBSplineMaxDegree = 0
  ExternalBSplineTolerance = 0
  ExternalGeometry = -> [Pocket007]
  FullyConstrained = true
  InternalTolerance = 1e-06
  InvalidShape = false
  MakeInternals = false
  MapMode = 5
  Placement = pos=(0,94,-3.37e-14) rot=(0,0.707107,0.707107;3.14159rad)
  Support = -> [Pocket007]
  TreeRank = 0
  ValidateShape = false
  sketch-geometry (9):
    g0: LineSegment StartX=7.36667 StartY=-15 StartZ=0 EndX=7.36667 EndY=-44.6482 EndZ=0
    g1: ArcOfCircle CenterX=17.3667 CenterY=-15 CenterZ=0 NormalX=0 NormalY=0 NormalZ=1 AngleXU=0 Radius=10 StartAngle=1.5708 EndAngle=3.14159
    g2: LineSegment StartX=17.3667 StartY=-5 StartZ=0 EndX=47.0149 EndY=-5 EndZ=0
    g3: ArcOfCircle CenterX=47.0149 CenterY=-10 CenterZ=0 NormalX=0 NormalY=0 NormalZ=1 AngleXU=0 Radius=5 StartAngle=5.49779 EndAngle=7.85398
    g4: ArcOfCircle CenterX=12.3667 CenterY=-44.6482 CenterZ=0 NormalX=0 NormalY=0 NormalZ=1 AngleXU=0 Radius=5 StartAngle=3.14159 EndAngle=5.49779
    g5: LineSegment StartX=50.5504 StartY=-13.5355 StartZ=0 EndX=15.9022 EndY=-48.1838 EndZ=0
    g6: LineSegment [constr] StartX=12.3667 StartY=-44.6482 StartZ=0 EndX=47.0149 EndY=-10 EndZ=0
    g7: Circle CenterX=47.0149 CenterY=-10 CenterZ=0 NormalX=0 NormalY=0 NormalZ=1 AngleXU=0 Radius=1.65
    g8: Circle CenterX=12.3667 CenterY=-44.6482 CenterZ=0 NormalX=0 NormalY=0 NormalZ=1 AngleXU=0 Radius=1.65
  constraints (20):
    c: Coincident(g0,g-4)
    c: Tangent(g1,g0) = -1.5708
    c: Coincident(g2,g1)
    c: Horizontal(g2)
    c: Coincident(g1,g-3)
    c: Tangent(g3,g2) = 1.5708
    c: Tangent(g5,g4) = 1.5708
    c: Tangent(g5,g3) = 1.5708
    c: Equal(g4,g3)
    c: Radius(g3) = 5
    c: Coincident(g6,g4)
    c: Coincident(g6,g3)
    c: Distance(g6) = 49
    c: Coincident(g7,g3)
    c: Coincident(g8,g4)
    c: Equal(g8,g7)
    c: Diameter(g7) = 3.3
    c: Tangent(g4,g0) = -1.5708
    c: Vertical(g0)
    c: Equal(g2,g0)
FEATURE [PartDesign::Pad] Pad008
  AddSubType = 0
  AutoTaperInnerAngle = true
  BaseFeature = -> Pocket007
  CheckUpToFaceLimits = true
  ClaimChildren = false
  Direction = (0,1,-4e-16)
  Fit = 0
  FitJoin = 0
  InnerFit = 0
  InnerFitJoin = 0
  InvalidShape = false
  Length = 3
  Length2 = 100
  NewSolid = false
  Profile = -> Sketch010
  Reversed = true
  Suppress = false
  TaperInnerAngle = 0
  TaperInnerAngleRev = 0
  TreeRank = 0
  Type = 0
  ValidateShape = true
  _ProfileBasedVersion = 0
FEATURE [Sketcher::SketchObject] Sketch020
  ArcFitTolerance = 0
  AttachmentSupport = -> [Pad008]
  ExternalBSplineMaxDegree = 0
  ExternalBSplineTolerance = 0
  FullyConstrained = false
  InternalTolerance = 1e-06
  InvalidShape = false
  MakeInternals = false
  MapMode = 5
  Placement = pos=(0,94,-5.73e-14) rot=(0,0.707107,0.707107;3.14159rad)
  Support = -> [Pad008]
  TreeRank = 0
  ValidateShape = false
  sketch-geometry (7):
    g0: LineSegment [constr] StartX=12.3667 StartY=-44.6482 StartZ=0 EndX=29.6908 EndY=-27.3241 EndZ=0
    g1: LineSegment [constr] StartX=47.0149 StartY=-10 StartZ=0 EndX=29.6908 EndY=-27.3241 EndZ=0
    g2: ArcOfCircle CenterX=29.6908 CenterY=-27.3241 CenterZ=0 NormalX=0 NormalY=0 NormalZ=1 AngleXU=0 Radius=7.5 StartAngle=1.85025 EndAngle=2.86214
    g3: LineSegment StartX=22.4817 StartY=-25.2554 StartZ=0 EndX=15.9022 EndY=-48.1838 EndZ=0
    g4: LineSegment StartX=27.6221 StartY=-20.1151 StartZ=0 EndX=50.5504 EndY=-13.5355 EndZ=0
    g5: LineSegment [constr] StartX=29.6908 StartY=-27.3241 StartZ=0 EndX=33.2263 EndY=-30.8597 EndZ=0
    g6: LineSegment StartX=15.9022 StartY=-48.1838 StartZ=0 EndX=50.5504 EndY=-13.5355 EndZ=0
  constraints (12):
    c: Coincident(g1,g0)
    c: Equal(g1,g0)
    c: Parallel(g1,g0)
    c: Coincident(g2,g0)
    c: Tangent(g4,g2) = 1.5708
    c: Tangent(g3,g2) = -1.5708
    c: Coincident(g5,g2)
    c: Perpendicular(g1,g5)
    c: Symmetric(g4,g3,g5)
    c: Radius(g2) = 7.5
    c: Coincident(g6,g3)
    c: Coincident(g6,g4)
FEATURE [PartDesign::Pocket] Pocket011
  AddSubType = 1
  AutoTaperInnerAngle = true
  BaseFeature = -> Pad008
  CheckUpToFaceLimits = true
  ClaimChildren = false
  Direction = (0,-1,7e-16)
  Fit = 0
  FitJoin = 0
  InnerFit = 0
  InnerFitJoin = 0
  InvalidShape = false
  Length = 5
  Length2 = 100
  NewSolid = false
  Profile = -> Sketch020
  Suppress = false
  TaperInnerAngle = 0
  TaperInnerAngleRev = 0
  TreeRank = 0
  Type = 1
  ValidateShape = true
  _ProfileBasedVersion = 0
  _Version = 0
FEATURE [PartDesign::Fillet] Fillet007
  AddSubType = 0
  Base = -> Pocket011 [Edge164,Edge178]
  BaseFeature = -> Pocket011
  InvalidShape = false
  NewSolid = false
  Radius = 4.5
  SupportTransform = true
  Suppress = false
  TreeRank = 0
  UseAllEdges = false
  ValidateShape = true
FEATURE [Sketcher::SketchObject] Sketch081
  ArcFitTolerance = 0
  AttachmentSupport = -> [Fillet007]
  ExternalBSplineMaxDegree = 0
  ExternalBSplineTolerance = 0
  FullyConstrained = true
  InternalTolerance = 1e-06
  InvalidShape = false
  MakeInternals = false
  MapMode = 5
  Placement = pos=(0,94,0) rot=(0,0.707107,0.707107;3.14159rad)
  Support = -> [Fillet007]
  TreeRank = 0
  ValidateShape = false
  sketch-geometry (4):
    g0: Circle CenterX=70 CenterY=2.5 CenterZ=0 NormalX=0 NormalY=0 NormalZ=1 AngleXU=0 Radius=2
    g1: Circle CenterX=132.5 CenterY=2.5 CenterZ=0 NormalX=0 NormalY=0 NormalZ=1 AngleXU=0 Radius=2
    g2: Circle CenterX=70 CenterY=2.5 CenterZ=0 NormalX=0 NormalY=0 NormalZ=1 AngleXU=0 Radius=4
    g3: Circle CenterX=132.5 CenterY=2.5 CenterZ=0 NormalX=0 NormalY=0 NormalZ=1 AngleXU=0 Radius=4
  constraints (10):
    c: DistanceX(g-1,g0) = 70
    c: DistanceX(g0,g1) = 62.5
    c: Equal(g1,g0)
    c: Diameter(g1) = 4
    c: DistanceY(g-1,g0) = 2.5
    c: Coincident(g2,g0)
    c: Coincident(g3,g1)
    c: Equal(g3,g2)
    c: Diameter(g3) = 8
    c: Horizontal(g1,g0)
FEATURE [PartDesign::Pad] Pad039
  AddSubType = 0
  AutoTaperInnerAngle = true
  BaseFeature = -> Fillet007
  CheckUpToFaceLimits = true
  ClaimChildren = false
  Direction = (0,1,-2e-16)
  Fit = 0
  FitJoin = 0
  InnerFit = 0
  InnerFitJoin = 0
  InvalidShape = false
  Length = 3
  Length2 = 100
  NewSolid = false
  Profile = -> Sketch081
  Suppress = false
  TaperInnerAngle = 0
  TaperInnerAngleRev = 0
  TreeRank = 0
  Type = 0
  ValidateShape = true
  _ProfileBasedVersion = 0
FEATURE [Sketcher::SketchObject] Sketch082
  ArcFitTolerance = 0
  AttachmentSupport = -> [Pad039]
  ExternalBSplineMaxDegree = 0
  ExternalBSplineTolerance = 0
  FullyConstrained = true
  InternalTolerance = 1e-06
  InvalidShape = false
  MakeInternals = false
  MapMode = 5
  Placement = pos=(0,94,0) rot=(0,0.707107,0.707107;3.14159rad)
  Support = -> [Pad039]
  TreeRank = 0
  ValidateShape = false
  sketch-geometry (2):
    g0: Circle CenterX=70 CenterY=2.5 CenterZ=0 NormalX=0 NormalY=0 NormalZ=1 AngleXU=0 Radius=2
    g1: Circle CenterX=132.5 CenterY=2.5 CenterZ=0 NormalX=0 NormalY=0 NormalZ=1 AngleXU=0 Radius=2
  constraints (6):
    c: Equal(g0,g1)
    c: Diameter(g1) = 4
    c: DistanceX(g0,g1) = 62.5
    c: DistanceX(g-1,g0) = 70
    c: DistanceY(g-1,g0) = 2.5
    c: Horizontal(g0,g1)
FEATURE [PartDesign::Pocket] Pocket045
  AddSubType = 1
  AutoTaperInnerAngle = true
  BaseFeature = -> Pad039
  CheckUpToFaceLimits = true
  ClaimChildren = false
  Direction = (0,-1,2e-16)
  Fit = 0
  FitJoin = 0
  InnerFit = 0
  InnerFitJoin = 0
  InvalidShape = false
  Length = 3
  Length2 = 100
  NewSolid = false
  Profile = -> Sketch082
  Suppress = false
  TaperInnerAngle = 0
  TaperInnerAngleRev = 0
  TreeRank = 0
  Type = 0
  ValidateShape = true
  _ProfileBasedVersion = 0
  _Version = 0
FEATURE [PartDesign::Chamfer] Chamfer030
  AddSubType = 0
  Angle = 45
  Base = -> Pocket045 [Edge65,Edge67]
  BaseFeature = -> Pocket045
  ChamferType = 0
  FlipDirection = false
  InvalidShape = false
  NewSolid = false
  Size = 2.9
  Size2 = 1
  SupportTransform = true
  Suppress = false
  TreeRank = 0
  UseAllEdges = false
  ValidateShape = true
FEATURE [PartDesign::Fillet] Fillet022
  AddSubType = 0
  Base = -> Chamfer030 [Edge25]
  BaseFeature = -> Chamfer030
  InvalidShape = false
  NewSolid = false
  Radius = 1.5
  SupportTransform = true
  Suppress = false
  TreeRank = 0
  UseAllEdges = false
  ValidateShape = true
FEATURE [PartDesign::Body] Body001
  AutoGroupSolids = false
  ClaimAllChildren = false
  ExportMode = 0
  Group = -> [Sketch018,Pad007,Pad006,Sketch017,Pad005,Mirrored003,Fillet006,Sketch016,Pad003,Mirrored002,Chamfer002,Sketch015,Pocket010,Sketch014,Pad004,Sketch013,Pocket009,Chamfer003,Sketch012,Pocket008,Sketch011,Pocket003,Pocket004,Sketch009,Pocket005,Pocket006,Pocket007,Sketch010,Pad008,Sketch020,Pocket011,Fillet007,Sketch081,Pad039,Sketch082,Pocket045,Chamfer030,Fillet022]
  InvalidShape = false
  Origin = -> Origin001
  SingleSolid = true
  Tip = -> Fillet022
  TreeRank = 0
  ValidateShape = false
  _ExportChildren = -> [Pad007,Pad006,Pad005,Mirrored003,Fillet006,Pad003,Mirrored002,Chamfer002,Pocket010,Pad004,Pocket009,Chamfer003,Pocket008,Pocket003,Pocket004,Pocket005,Pocket006,Pocket007,Pad008,Pocket011,Fillet007,Pad039,Pocket045,Chamfer030,Fillet022]
  _GroupVersion = 1
COMPONENT P2 — recipe-attached ("Body002", modeled in this document).
Construction recipe (the document's own serialized feature program — sketch geometry with constraints, then the solid features built on it; lengths are millimeters unless a unit is written):

FEATURE [Sketcher::SketchObject] Sketch026
  ArcFitTolerance = 0
  AttachmentSupport = -> [XY_Plane002]
  ExternalBSplineMaxDegree = 0
  ExternalBSplineTolerance = 0
  FullyConstrained = false
  InternalTolerance = 1e-06
  InvalidShape = false
  MakeInternals = false
  MapMode = 5
  Support = -> [XY_Plane002]
  TreeRank = 0
  ValidateShape = false
  sketch-geometry (1):
    g0: Circle CenterX=0 CenterY=0 CenterZ=0 NormalX=0 NormalY=0 NormalZ=1 AngleXU=0 Radius=21
  constraints (2):
    c: Coincident(g0,g-1)
    c: Diameter(g0) = 42
FEATURE [PartDesign::Pad] Pad015
  AddSubType = 0
  AutoTaperInnerAngle = true
  CheckUpToFaceLimits = true
  ClaimChildren = false
  Direction = (1,1,1)
  Fit = 0
  FitJoin = 0
  InnerFit = 0
  InnerFitJoin = 0
  InvalidShape = false
  Length = 22.25
  Length2 = 100
  Midplane = true
  NewSolid = false
  Profile = -> Sketch026
  Suppress = false
  TaperInnerAngle = 0
  TaperInnerAngleRev = 0
  TreeRank = 0
  Type = 0
  ValidateShape = true
  _ProfileBasedVersion = 0
FEATURE [Sketcher::SketchObject] Sketch027
  ArcFitTolerance = 0
  AttachmentSupport = -> [Pad015]
  ExternalBSplineMaxDegree = 0
  ExternalBSplineTolerance = 0
  FullyConstrained = false
  InternalTolerance = 1e-06
  InvalidShape = false
  MakeInternals = false
  MapMode = 5
  Placement = pos=(0,0,-11.125) rot=(1,0,0;3.14159rad)
  Support = -> [Pad015]
  TreeRank = 0
  ValidateShape = false
  sketch-geometry (1):
    g0: Circle CenterX=0 CenterY=0 CenterZ=0 NormalX=0 NormalY=0 NormalZ=1 AngleXU=0 Radius=4.95
  constraints (2):
    c: Coincident(g0,g-1)
    c: Diameter(g0) = 9.9
FEATURE [PartDesign::Pad] Pad016
  AddSubType = 0
  AutoTaperInnerAngle = true
  BaseFeature = -> Pad015
  CheckUpToFaceLimits = true
  ClaimChildren = false
  Direction = (1,1,1)
  Fit = 0
  FitJoin = 0
  InnerFit = 0
  InnerFitJoin = 0
  InvalidShape = false
  Length = 1.5
  Length2 = 100
  NewSolid = false
  Profile = -> Sketch027
  Suppress = false
  TaperInnerAngle = 0
  TaperInnerAngleRev = 0
  TreeRank = 0
  Type = 0
  ValidateShape = true
  _ProfileBasedVersion = 0
FEATURE [Sketcher::SketchObject] Sketch028
  ArcFitTolerance = 0
  AttachmentSupport = -> [Plane003]
  ExternalBSplineMaxDegree = 0
  ExternalBSplineTolerance = 0
  ExternalGeometry = -> [Pad016]
  FullyConstrained = false
  InternalTolerance = 1e-06
  InvalidShape = false
  MakeInternals = false
  MapMode = 5
  Placement = pos=(0,0,-8.73) rot=(1,0,0;3.14159rad)
  Support = -> [Plane003]
  TreeRank = 0
  ValidateShape = false
  sketch-geometry (5):
    g0: ArcOfCircle CenterX=0 CenterY=0 CenterZ=0 NormalX=0 NormalY=0 NormalZ=1 AngleXU=0 Radius=21 StartAngle=1.26361 EndAngle=1.87799
    g1: LineSegment StartX=-6.35 StartY=20.0169 StartZ=0 EndX=-6.35 EndY=26.5 EndZ=0
    g2: LineSegment StartX=-6.35 StartY=26.5 StartZ=0 EndX=6.35 EndY=26.5 EndZ=0
    g3: LineSegment StartX=6.35 StartY=26.5 StartZ=0 EndX=6.35 EndY=20.0169 EndZ=0
    g4: LineSegment [constr] StartX=0 StartY=26.5 StartZ=0 EndX=0 EndY=21 EndZ=0
  constraints (16):
    c: Coincident(g0,g-1)
    c: PointOnObject(g0,g-3)
    c: Coincident(g0,g1)
    c: Coincident(g1,g2)
    c: Horizontal(g2)
    c: Coincident(g2,g3)
    c: Coincident(g3,g0)
    c: Vertical(g3)
    c: Symmetric(g0,g0,g-2)
    c: Vertical(g1)
    c: DistanceX(g2,g2) = 12.7
    c: PointOnObject(g4,g-2)
    c: PointOnObject(g4,g0)
    c: PointOnObject(g4,g-2)
    c: PointOnObject(g4,g2)
    c: DistanceY(g4,g4) = 5.5
FEATURE [PartDesign::Pad] Pad009
  AddSubType = 0
  AutoTaperInnerAngle = true
  BaseFeature = -> Pad016
  CheckUpToFaceLimits = true
  ClaimChildren = false
  Direction = (1,1,1)
  Fit = 0
  FitJoin = 0
  InnerFit = 0
  InnerFitJoin = 0
  InvalidShape = false
  Length = 11.8
  Length2 = 100
  NewSolid = false
  Profile = -> Sketch028
  Reversed = true
  Suppress = false
  TaperInnerAngle = 0
  TaperInnerAngleRev = 0
  TreeRank = 0
  Type = 0
  ValidateShape = true
  _ProfileBasedVersion = 0
FEATURE [Sketcher::SketchObject] Sketch021
  ArcFitTolerance = 0
  AttachmentSupport = -> [Pad009]
  ExternalBSplineMaxDegree = 0
  ExternalBSplineTolerance = 0
  ExternalGeometry = -> [Pad009]
  FullyConstrained = false
  InternalTolerance = 1e-06
  InvalidShape = false
  MakeInternals = false
  MapMode = 5
  Placement = pos=(0,9e-16,3.07) rot=(0,0,1;0rad)
  Support = -> [Pad009]
  TreeRank = 0
  ValidateShape = false
  sketch-geometry (4):
    g0: ArcOfCircle CenterX=-4.3e-15 CenterY=-1e-16 CenterZ=0 NormalX=0 NormalY=0 NormalZ=1 AngleXU=0 Radius=21 StartAngle=4.4052 EndAngle=5.01958
    g1: ArcOfCircle CenterX=-4.3e-15 CenterY=-1e-16 CenterZ=0 NormalX=0 NormalY=0 NormalZ=1 AngleXU=0 Radius=21.7161 StartAngle=4.41564 EndAngle=5.00914
    g2: LineSegment StartX=-6.35 StartY=-20.0169 StartZ=0 EndX=-6.35 EndY=-20.7669 EndZ=0
    g3: LineSegment StartX=6.35 StartY=-20.0169 StartZ=0 EndX=6.35 EndY=-20.7669 EndZ=0
  constraints (11):
    c: Coincident(g0,g-3)
    c: Coincident(g0,g-3)
    c: Equal(g-3,g0)
    c: Coincident(g1,g0)
    c: Coincident(g2,g0)
    c: Vertical(g2)
    c: Coincident(g3,g0)
    c: Vertical(g3)
    c: Coincident(g1,g2)
    c: Coincident(g3,g1)
    c: DistanceY(g3,g3) = 0.75
FEATURE [PartDesign::Pad] Pad010
  AddSubType = 0
  AutoTaperInnerAngle = true
  BaseFeature = -> Pad009
  CheckUpToFaceLimits = true
  ClaimChildren = false
  Direction = (1,1,1)
  Fit = 0
  FitJoin = 0
  InnerFit = 0
  InnerFitJoin = 0
  InvalidShape = false
  Length = 2.2
  Length2 = 100
  NewSolid = false
  Profile = -> Sketch021
  Suppress = false
  TaperInnerAngle = 0
  TaperInnerAngleRev = 0
  TreeRank = 0
  Type = 0
  ValidateShape = true
  _ProfileBasedVersion = 0
FEATURE [Sketcher::SketchObject] Sketch022
  ArcFitTolerance = 0
  AttachmentSupport = -> [Pad010]
  ExternalBSplineMaxDegree = 0
  ExternalBSplineTolerance = 0
  ExternalGeometry = -> [Pad010]
  FullyConstrained = false
  InternalTolerance = 1e-06
  InvalidShape = false
  MakeInternals = false
  MapMode = 5
  Placement = pos=(0,0,11.125) rot=(0,0,1;0rad)
  Support = -> [Pad010]
  TreeRank = 0
  ValidateShape = false
  sketch-geometry (12):
    g0: Circle CenterX=24.5 CenterY=0 CenterZ=0 NormalX=0 NormalY=0 NormalZ=1 AngleXU=0 Radius=1.5
    g1: ArcOfCircle CenterX=24.5 CenterY=0 CenterZ=0 NormalX=0 NormalY=0 NormalZ=1 AngleXU=0 Radius=4.25 StartAngle=5.46517 EndAngle=7.1012
    g2: LineSegment StartX=27.4056 StartY=3.1016 StartZ=0 EndX=14.3571 EndY=15.3255 EndZ=0
    g3: LineSegment StartX=27.4056 StartY=-3.1016 StartZ=0 EndX=14.3571 EndY=-15.3255 EndZ=0
    g4: Circle CenterX=-24.5 CenterY=0 CenterZ=0 NormalX=0 NormalY=0 NormalZ=1 AngleXU=0 Radius=1.5
    g5: ArcOfCircle CenterX=-24.5 CenterY=0 CenterZ=0 NormalX=0 NormalY=0 NormalZ=1 AngleXU=0 Radius=4.25 StartAngle=2.32358 EndAngle=3.9596
    g6: LineSegment StartX=-27.4056 StartY=-3.1016 StartZ=0 EndX=-14.3571 EndY=-15.3256 EndZ=0
    g7: LineSegment StartX=-27.4056 StartY=3.1016 StartZ=0 EndX=-14.3571 EndY=15.3255 EndZ=0
    g8: GeomPoint [constr] X=-28.75 Y=0 Z=0
    g9: GeomPoint [constr] X=28.75 Y=0 Z=0
    g10: ArcOfCircle CenterX=2.3e-15 CenterY=-1.1e-15 CenterZ=0 NormalX=0 NormalY=0 NormalZ=1 AngleXU=0 Radius=21 StartAngle=2.32358 EndAngle=3.95961
    g11: ArcOfCircle CenterX=4e-16 CenterY=-1.3e-15 CenterZ=0 NormalX=0 NormalY=0 NormalZ=1 AngleXU=0 Radius=21 StartAngle=5.46517 EndAngle=7.1012
  constraints (30):
    c: PointOnObject(g0,g-1)
    c: Coincident(g1,g0)
    c: Diameter(g0) = 3
    c: PointOnObject(g2,g-3)
    c: PointOnObject(g3,g-3)
    c: Tangent(g2,g-3)
    c: Tangent(g3,g-3)
    c: Coincident(g5,g4)
    c: PointOnObject(g7,g-3)
    c: PointOnObject(g6,g-3)
    c: Tangent(g7,g-3)
    c: Tangent(g7,g5) = 1.5708
    c: Tangent(g6,g5) = -1.5708
    c: Equal(g4,g0)
    c: Symmetric(g4,g0,g-2)
    c: Tangent(g2,g1) = -1.5708
    c: Tangent(g3,g1) = 1.5708
    c: DistanceX(g4,g0) = 49
    c: Symmetric(g5,g1,g-2)
    c: PointOnObject(g8,g-1)
    c: PointOnObject(g8,g5)
    c: PointOnObject(g9,g-1)
    c: PointOnObject(g9,g1)
    c: DistanceX(g8,g9) = 57.5
    c: Coincident(g10,g7)
    c: Coincident(g10,g6)
    c: Equal(g10,g-3)
    c: Coincident(g11,g2)
    c: Coincident(g11,g3)
    c: Equal(g11,g-3)
FEATURE [PartDesign::Pad] Pad011
  AddSubType = 0
  AutoTaperInnerAngle = true
  BaseFeature = -> Pad010
  CheckUpToFaceLimits = true
  ClaimChildren = false
  Direction = (1,1,1)
  Fit = 0
  FitJoin = 0
  InnerFit = 0
  InnerFitJoin = 0
  InvalidShape = false
  Length = 1
  Length2 = 100
  NewSolid = false
  Profile = -> Sketch022
  Reversed = true
  Suppress = false
  TaperInnerAngle = 0
  TaperInnerAngleRev = 0
  TreeRank = 0
  Type = 0
  ValidateShape = true
  _ProfileBasedVersion = 0
FEATURE [Sketcher::SketchObject] Sketch023
  ArcFitTolerance = 0
  AttachmentSupport = -> [Pad011]
  ExternalBSplineMaxDegree = 0
  ExternalBSplineTolerance = 0
  ExternalGeometry = -> [Pad011]
  FullyConstrained = false
  InternalTolerance = 1e-06
  InvalidShape = false
  MakeInternals = false
  MapMode = 5
  Placement = pos=(0,0,11.125) rot=(0,0,1;0rad)
  Support = -> [Pad011]
  TreeRank = 0
  ValidateShape = false
  sketch-geometry (1):
    g0: Circle CenterX=0 CenterY=0 CenterZ=0 NormalX=0 NormalY=0 NormalZ=1 AngleXU=0 Radius=4.95
  constraints (2):
    c: Coincident(g0,g-1)
    c: Equal(g-3,g0)
FEATURE [PartDesign::Pad] Pad012
  AddSubType = 0
  AutoTaperInnerAngle = true
  BaseFeature = -> Pad011
  CheckUpToFaceLimits = true
  ClaimChildren = false
  Direction = (1,1,1)
  Fit = 0
  FitJoin = 0
  InnerFit = 0
  InnerFitJoin = 0
  InvalidShape = false
  Length = 1.5
  Length2 = 100
  NewSolid = false
  Profile = -> Sketch023
  Suppress = false
  TaperInnerAngle = 0
  TaperInnerAngleRev = 0
  TreeRank = 0
  Type = 0
  ValidateShape = true
  _ProfileBasedVersion = 0
FEATURE [Sketcher::SketchObject] Sketch024
  ArcFitTolerance = 0
  AttachmentSupport = -> [Pad012]
  ExternalBSplineMaxDegree = 0
  ExternalBSplineTolerance = 0
  FullyConstrained = false
  InternalTolerance = 1e-06
  InvalidShape = false
  MakeInternals = false
  MapMode = 5
  Placement = pos=(0,0,12.625) rot=(0,0,1;0rad)
  Support = -> [Pad012]
  TreeRank = 0
  ValidateShape = false
  sketch-geometry (1):
    g0: Circle CenterX=0 CenterY=0 CenterZ=0 NormalX=0 NormalY=0 NormalZ=1 AngleXU=0 Radius=1.5
  constraints (2):
    c: Coincident(g0,g-1)
    c: Diameter(g0) = 3
FEATURE [PartDesign::Pad] Pad013
  AddSubType = 0
  AutoTaperInnerAngle = true
  BaseFeature = -> Pad012
  CheckUpToFaceLimits = true
  ClaimChildren = false
  Direction = (1,1,1)
  Fit = 0
  FitJoin = 0
  InnerFit = 0
  InnerFitJoin = 0
  InvalidShape = false
  Length = 2
  Length2 = 100
  NewSolid = false
  Profile = -> Sketch024
  Suppress = false
  TaperInnerAngle = 0
  TaperInnerAngleRev = 0
  TreeRank = 0
  Type = 0
  ValidateShape = true
  _ProfileBasedVersion = 0
FEATURE [PartDesign::Pad] Pad014
  AddSubType = 0
  AutoTaperInnerAngle = true
  BaseFeature = -> Pad013
  CheckUpToFaceLimits = true
  ClaimChildren = false
  Direction = (1,1,1)
  Fit = 0
  FitJoin = 0
  InnerFit = 0
  InnerFitJoin = 0
  InvalidShape = false
  Length = 8
  Length2 = 100
  NewSolid = false
  Profile = -> InvoluteGear
  Suppress = false
  TaperInnerAngle = 0
  TaperInnerAngleRev = 0
  TreeRank = 0
  Type = 0
  ValidateShape = true
  _ProfileBasedVersion = 0
FEATURE [Sketcher::SketchObject] Sketch025
  ArcFitTolerance = 0
  AttachmentSupport = -> [Pad013]
  ExternalBSplineMaxDegree = 0
  ExternalBSplineTolerance = 0
  FullyConstrained = true
  InternalTolerance = 1e-06
  InvalidShape = false
  MakeInternals = false
  MapMode = 5
  Placement = pos=(0,0,14.625) rot=(0,0,1;0rad)
  Support = -> [Pad013]
  TreeRank = 0
  ValidateShape = false
FEATURE [PartDesign::Body] Body002
  AutoGroupSolids = false
  ClaimAllChildren = false
  ExportMode = 0
  Group = -> [Sketch026,Pad015,Sketch027,Pad016,Sketch028,Pad009,Sketch021,Pad010,Sketch022,Pad011,Sketch023,Pad012,Sketch024,Pad013,Sketch025,Pad014]
  InvalidShape = false
  Origin = -> Origin002
  SingleSolid = true
  Tip = -> Pad014
  TreeRank = 0
  ValidateShape = false
  _ExportChildren = -> [Pad015,Pad016,Pad009,Pad010,Pad011,Pad012,Pad013,Sketch025,Pad014]
  _GroupVersion = 1
COMPONENT P3 — recipe-attached ("Body003", modeled in this document).
Construction recipe (the document's own serialized feature program — sketch geometry with constraints, then the solid features built on it; lengths are millimeters unless a unit is written):

FEATURE [Sketcher::SketchObject] Sketch029
  ArcFitTolerance = 0
  AttachmentSupport = -> [XY_Plane003]
  ExternalBSplineMaxDegree = 0
  ExternalBSplineTolerance = 0
  FullyConstrained = false
  InternalTolerance = 1e-06
  InvalidShape = false
  MakeInternals = false
  MapMode = 5
  Support = -> [XY_Plane003]
  TreeRank = 0
  ValidateShape = false
  sketch-geometry (1):
    g0: Circle CenterX=0 CenterY=0 CenterZ=0 NormalX=0 NormalY=0 NormalZ=1 AngleXU=0 Radius=15
  constraints (2):
    c: Coincident(g0,g-1)
    c: Diameter(g0) = 30
FEATURE [PartDesign::Pad] Pad017
  AddSubType = 0
  AutoTaperInnerAngle = true
  CheckUpToFaceLimits = true
  ClaimChildren = false
  Direction = (1,1,1)
  Fit = 0
  FitJoin = 0
  InnerFit = 0
  InnerFitJoin = 0
  InvalidShape = false
  Length = 8
  Length2 = 100
  NewSolid = false
  Profile = -> Sketch029
  Suppress = false
  TaperInnerAngle = 0
  TaperInnerAngleRev = 0
  TreeRank = 0
  Type = 0
  ValidateShape = true
  _ProfileBasedVersion = 0
FEATURE [Sketcher::SketchObject] Sketch030
  ArcFitTolerance = 0
  AttachmentSupport = -> [Pad017]
  ExternalBSplineMaxDegree = 0
  ExternalBSplineTolerance = 0
  FullyConstrained = false
  InternalTolerance = 1e-06
  InvalidShape = false
  MakeInternals = false
  MapMode = 5
  Placement = pos=(0,0,8) rot=(0,0,1;0rad)
  Support = -> [Pad017]
  TreeRank = 0
  ValidateShape = false
  sketch-geometry (1):
    g0: Circle CenterX=0 CenterY=0 CenterZ=0 NormalX=0 NormalY=0 NormalZ=1 AngleXU=0 Radius=2
  constraints (2):
    c: Coincident(g0,g-1)
    c: Diameter(g0) = 4
FEATURE [PartDesign::Pocket] Pocket012
  AddSubType = 1
  AutoTaperInnerAngle = true
  BaseFeature = -> Pad017
  CheckUpToFaceLimits = true
  ClaimChildren = false
  Direction = (1,1,1)
  Fit = 0
  FitJoin = 0
  InnerFit = 0
  InnerFitJoin = 0
  InvalidShape = false
  Length = 6
  Length2 = 100
  NewSolid = false
  Profile = -> Sketch030
  Suppress = false
  TaperInnerAngle = 0
  TaperInnerAngleRev = 0
  TreeRank = 0
  Type = 0
  ValidateShape = true
  _ProfileBasedVersion = 0
  _Version = 0
FEATURE [PartDesign::SubShapeBinder] Binder
  BindCopyOnChange = 0
  BindMode = 0
  ClaimChildren = false
  Context = -> Assembly002 [Parts002.Assembly004.Parts004.Body003.Binder.]
  EdgeTolerance = 1e-06
  FillStyle = 0
  Fuse = false
  InvalidShape = false
  MakeFace = true
  MergeEdges = true
  OffsetFill = false
  OffsetIntersection = false
  OffsetJoinType = 0
  OffsetOpenResult = false
  Outline = false
  PartialLoad = false
  Refine = true
  Relative = true
  SplitEdges = false
  Support = -> [Assembly003[Parts003.Body002.Pad014.Face201]]
  TightBound = false
  TreeRank = 0
  ValidateShape = false
  _Version = 3
FEATURE [PartDesign::Pocket] Pocket013
  AddSubType = 1
  AutoTaperInnerAngle = true
  BaseFeature = -> Pocket012
  CheckUpToFaceLimits = true
  ClaimChildren = false
  Direction = (1,1,1)
  Fit = 0
  FitJoin = 0
  InnerFit = 0
  InnerFitJoin = 0
  InvalidShape = false
  Length = 5
  Length2 = 100
  NewSolid = false
  Profile = -> Binder
  Suppress = false
  TaperInnerAngle = 0
  TaperInnerAngleRev = 0
  TreeRank = 0
  Type = 1
  ValidateShape = true
  _ProfileBasedVersion = 0
  _Version = 0
FEATURE [PartDesign::Chamfer] Chamfer
  AddSubType = 0
  Angle = 45
  Base = -> Pocket013 [Edge86,Edge81,Edge76,Edge71,Edge66,Edge61,Edge56,Edge51,Edge46,Edge41,Edge36,Edge31,Edge26,Edge21,Edge16,Edge11,Edge6,Edge171,Edge166,Edge161,Edge156,Edge151,Edge146,Edge141,Edge136,Edge131,Edge126,Edge121,Edge116,Edge111,Edge106,Edge101,Edge96,Edge91]
  BaseFeature = -> Pocket013
  ChamferType = 1
  FlipDirection = false
  InvalidShape = false
  NewSolid = false
  Size = 0.15
  Size2 = 5.9
  SupportTransform = true
  Suppress = false
  TreeRank = 0
  UseAllEdges = false
  ValidateShape = true
FEATURE [PartDesign::Body] Body003
  AutoGroupSolids = false
  ClaimAllChildren = false
  ExportMode = 0
  Group = -> [Sketch029,Pad017,Sketch030,Pocket012,Binder,Pocket013,Chamfer]
  InvalidShape = false
  Origin = -> Origin003
  SingleSolid = true
  Tip = -> Chamfer
  TreeRank = 0
  ValidateShape = false
  _ExportChildren = -> [Pad017,Pocket012,Pocket013,Chamfer]
  _GroupVersion = 1
COMPONENT P4 — recipe-attached ("Body004", modeled in this document).
Construction recipe (the document's own serialized feature program — sketch geometry with constraints, then the solid features built on it; lengths are millimeters unless a unit is written):

FEATURE [Sketcher::SketchObject] Sketch031
  ArcFitTolerance = 0
  AttachmentSupport = -> [XY_Plane004]
  ExternalBSplineMaxDegree = 0
  ExternalBSplineTolerance = 0
  FullyConstrained = false
  InternalTolerance = 1e-06
  InvalidShape = false
  MakeInternals = false
  MapMode = 5
  Support = -> [XY_Plane004]
  TreeRank = 0
  ValidateShape = false
  sketch-geometry (16):
    g0: LineSegment StartX=-154 StartY=89 StartZ=0 EndX=154 EndY=89 EndZ=0
    g1: LineSegment StartX=164 StartY=79 StartZ=0 EndX=164 EndY=-79 EndZ=0
    g2: LineSegment StartX=154 StartY=-89 StartZ=0 EndX=-154 EndY=-89 EndZ=0
    g3: LineSegment StartX=-164 StartY=-79 StartZ=0 EndX=-164 EndY=79 EndZ=0
    g4: ArcOfCircle CenterX=-154 CenterY=79 CenterZ=0 NormalX=0 NormalY=0 NormalZ=1 AngleXU=0 Radius=10 StartAngle=1.5708 EndAngle=3.14159
    g5: ArcOfCircle CenterX=154 CenterY=79 CenterZ=0 NormalX=0 NormalY=0 NormalZ=1 AngleXU=0 Radius=10 StartAngle=-9e-16 EndAngle=1.5708
    g6: ArcOfCircle CenterX=154 CenterY=-79 CenterZ=0 NormalX=0 NormalY=0 NormalZ=1 AngleXU=0 Radius=10 StartAngle=4.71239 EndAngle=6.28319
    g7: ArcOfCircle CenterX=-154 CenterY=-79 CenterZ=0 NormalX=0 NormalY=0 NormalZ=1 AngleXU=0 Radius=10 StartAngle=3.14159 EndAngle=4.71239
    g8: LineSegment StartX=-154 StartY=94 StartZ=0 EndX=154 EndY=94 EndZ=0
    g9: LineSegment StartX=169 StartY=79 StartZ=0 EndX=169 EndY=-79 EndZ=0
    g10: LineSegment StartX=154 StartY=-94 StartZ=0 EndX=-154 EndY=-94 EndZ=0
    g11: LineSegment StartX=-169 StartY=-79 StartZ=0 EndX=-169 EndY=79 EndZ=0
    g12: ArcOfCircle CenterX=-154 CenterY=79 CenterZ=0 NormalX=0 NormalY=0 NormalZ=1 AngleXU=0 Radius=15 StartAngle=1.5708 EndAngle=3.14159
    g13: ArcOfCircle CenterX=154 CenterY=79 CenterZ=0 NormalX=0 NormalY=0 NormalZ=1 AngleXU=0 Radius=15 StartAngle=1e-16 EndAngle=1.5708
    g14: ArcOfCircle CenterX=154 CenterY=-79 CenterZ=0 NormalX=0 NormalY=0 NormalZ=1 AngleXU=0 Radius=15 StartAngle=4.71239 EndAngle=6.28319
    g15: ArcOfCircle CenterX=-154 CenterY=-79 CenterZ=0 NormalX=0 NormalY=0 NormalZ=1 AngleXU=0 Radius=15 StartAngle=3.14159 EndAngle=4.71239
  constraints (35):
    c: Tangent(g3,g4) = 1.5708
    c: Tangent(g0,g4) = 1.5708
    c: Tangent(g0,g5) = 1.5708
    c: Tangent(g1,g5) = 1.5708
    c: Tangent(g1,g6) = 1.5708
    c: Tangent(g2,g6) = 1.5708
    c: Tangent(g2,g7) = 1.5708
    c: Tangent(g3,g7) = 1.5708
    c: Equal(g5,g6)
    c: Equal(g6,g7)
    c: Equal(g7,g4)
    c: Symmetric(g3,g1,g-2)
    c: Symmetric(g3,g1,g-2)
    c: Symmetric(g3,g3,g-1)
    c: DistanceX(g3,g1) = 328
    c: DistanceY(g2,g0) = 178
    c: Radius(g5) = 10
    c: Tangent(g11,g12) = 1.5708
    c: Tangent(g8,g12) = 1.5708
    c: Tangent(g8,g13) = 1.5708
    c: Tangent(g9,g13) = 1.5708
    c: Tangent(g9,g14) = 1.5708
    c: Tangent(g10,g14) = 1.5708
    c: Tangent(g10,g15) = 1.5708
    c: Tangent(g11,g15) = 1.5708
    c: Horizontal(g8)
    c: Horizontal(g10)
    c: Vertical(g9)
    c: Vertical(g11)
    c: DistanceX(g11,g3) = 5
    c: DistanceY(g0,g8) = 5
    c: Equal(g14,g13)
    c: Equal(g13,g12)
    c: Coincident(g15,g7)
    c: Coincident(g13,g5)
FEATURE [PartDesign::Pad] Pad018
  AddSubType = 0
  AutoTaperInnerAngle = true
  CheckUpToFaceLimits = true
  ClaimChildren = false
  Direction = (1,1,1)
  Fit = 0
  FitJoin = 0
  InnerFit = 0
  InnerFitJoin = 0
  InvalidShape = false
  Length = 10
  Length2 = 100
  NewSolid = false
  Profile = -> Sketch031
  Suppress = false
  TaperInnerAngle = 0
  TaperInnerAngleRev = 0
  TreeRank = 0
  Type = 0
  ValidateShape = true
  _ProfileBasedVersion = 0
FEATURE [PartDesign::Pad] Pad019
  AddSubType = 0
  AutoTaperInnerAngle = true
  BaseFeature = -> Pad018
  CheckUpToFaceLimits = true
  ClaimChildren = false
  Direction = (1,1,1)
  Fit = 0
  FitJoin = 0
  InnerFit = 0
  InnerFitJoin = 0
  InvalidShape = false
  Length = 5
  Length2 = 100
  NewSolid = false
  Profile = -> Sketch032
  Reversed = true
  Suppress = false
  TaperInnerAngle = 0
  TaperInnerAngleRev = 0
  TreeRank = 0
  Type = 0
  ValidateShape = true
  _ProfileBasedVersion = 0
FEATURE [Sketcher::SketchObject] Sketch033
  ArcFitTolerance = 0
  AttachmentSupport = -> [Pad019]
  ExternalBSplineMaxDegree = 0
  ExternalBSplineTolerance = 0
  ExternalGeometry = -> [Pad019]
  FullyConstrained = false
  InternalTolerance = 1e-06
  InvalidShape = false
  MakeInternals = false
  MapMode = 5
  Placement = pos=(0,94,0) rot=(0,0.707107,0.707107;3.14159rad)
  Support = -> [Pad019]
  TreeRank = 0
  ValidateShape = false
  sketch-geometry (6):
    g0: LineSegment StartX=-7.36667 StartY=-5 StartZ=0 EndX=7.36667 EndY=-5 EndZ=0
    g1: LineSegment StartX=-7.36667 StartY=-5 StartZ=0 EndX=-7.36667 EndY=-45 EndZ=0
    g2: LineSegment StartX=7.36667 StartY=-45 StartZ=0 EndX=7.36667 EndY=-5 EndZ=0
    g3: ArcOfCircle CenterX=5.36667 CenterY=-45 CenterZ=0 NormalX=0 NormalY=0 NormalZ=1 AngleXU=0 Radius=2 StartAngle=2.77438 EndAngle=6.28319
    g4: ArcOfCircle CenterX=-1e-16 CenterY=-42.9357 CenterZ=0 NormalX=0 NormalY=0 NormalZ=1 AngleXU=0 Radius=3.75 StartAngle=5.91598 EndAngle=9.79199
    g5: ArcOfCircle CenterX=-5.36667 CenterY=-45 CenterZ=0 NormalX=0 NormalY=0 NormalZ=1 AngleXU=0 Radius=2 StartAngle=3.14159 EndAngle=6.65039
  constraints (15):
    c: Symmetric(g0,g0,g-2)
    c: Coincident(g1,g0)
    c: Vertical(g1)
    c: Coincident(g2,g0)
    c: PointOnObject(g0,g-4)
    c: Symmetric(g2,g1,g-2)
    c: Tangent(g3,g2) = -1.5708
    c: Coincident(g5,g4)
    c: Tangent(g1,g5) = -1.5708
    c: Symmetric(g3,g4,g-2)
    c: Tangent(g4,g3) = 1.5708
    c: Diameter(g4) = 7.5
    c: Radius(g3) = 2
    c: DistanceX(g4,g3) = 7
    c: DistanceY(g1,g1) = 40
FEATURE [PartDesign::Pad] Pad020
  AddSubType = 0
  AutoTaperInnerAngle = true
  BaseFeature = -> Pad019
  CheckUpToFaceLimits = true
  ClaimChildren = false
  Direction = (1,1,1)
  Fit = 0
  FitJoin = 0
  InnerFit = 0
  InnerFitJoin = 0
  InvalidShape = false
  Length = 10
  Length2 = 100
  NewSolid = false
  Profile = -> Sketch033
  Reversed = true
  Suppress = false
  TaperInnerAngle = 0
  TaperInnerAngleRev = 0
  TreeRank = 0
  Type = 3
  UpToFace = -> Pad019 [Face27]
  ValidateShape = true
  _ProfileBasedVersion = 0
FEATURE [PartDesign::Mirrored] Mirrored004
  AddSubType = 0
  BaseFeature = -> Pad020
  CopyShape = true
  InvalidShape = false
  MirrorPlane = -> XZ_Plane004
  NewSolid = false
  OriginalSubs = -> [Pad020]
  Originals = -> [Pad020]
  ParallelTransform = true
  SubTransform = true
  Suppress = false
  TreeRank = 0
  ValidateShape = true
  _Version = 0
FEATURE [PartDesign::Fillet] Fillet008
  AddSubType = 0
  Base = -> Mirrored004 [Edge100,Edge42,Edge36,Edge104]
  BaseFeature = -> Mirrored004
  InvalidShape = false
  NewSolid = false
  Radius = 10
  SupportTransform = true
  Suppress = false
  TreeRank = 0
  UseAllEdges = false
  ValidateShape = true
FEATURE [Sketcher::SketchObject] Sketch035
  ArcFitTolerance = 0
  ExternalBSplineMaxDegree = 0
  ExternalBSplineTolerance = 0
  FullyConstrained = false
  InternalTolerance = 1e-06
  InvalidShape = false
  MakeInternals = false
  MapMode = 5
  Placement = pos=(0,0,10) rot=(0,0,1;0rad)
  TreeRank = 0
  ValidateShape = false
  sketch-geometry (4):
    g0: LineSegment StartX=0 StartY=119.45 StartZ=0 EndX=0 EndY=-119.45 EndZ=0
    g1: LineSegment StartX=0 StartY=119.45 StartZ=0 EndX=200.233 EndY=119.45 EndZ=0
    g2: LineSegment StartX=200.233 StartY=119.45 StartZ=0 EndX=200.233 EndY=-119.45 EndZ=0
    g3: LineSegment StartX=200.233 StartY=-119.45 StartZ=0 EndX=0 EndY=-119.45 EndZ=0
  constraints (9):
    c: PointOnObject(g0,g-2)
    c: Symmetric(g0,g0,g-1)
    c: Coincident(g0,g1)
    c: Horizontal(g1)
    c: Coincident(g1,g2)
    c: Vertical(g2)
    c: Coincident(g2,g3)
    c: Coincident(g3,g0)
    c: Horizontal(g3)
FEATURE [Sketcher::SketchObject] Sketch034
  ArcFitTolerance = 0
  AttachmentSupport = -> [Fillet008]
  ExternalBSplineMaxDegree = 0
  ExternalBSplineTolerance = 0
  ExternalGeometry = -> [Fillet008]
  FullyConstrained = false
  InternalTolerance = 1e-06
  InvalidShape = false
  MakeInternals = false
  MapMode = 5
  Placement = pos=(0,94,-3.38e-14) rot=(0,0.707107,0.707107;3.14159rad)
  Support = -> [Fillet008]
  TreeRank = 0
  ValidateShape = false
  sketch-geometry (4):
    g0: LineSegment StartX=-5.36666 StartY=-47 StartZ=0 EndX=5.36667 EndY=-47 EndZ=0
    g1: ArcOfCircle CenterX=-5.36667 CenterY=-45 CenterZ=0 NormalX=0 NormalY=0 NormalZ=1 AngleXU=0 Radius=2 StartAngle=4.71239 EndAngle=6.65039
    g2: ArcOfCircle CenterX=5.36667 CenterY=-45 CenterZ=0 NormalX=0 NormalY=0 NormalZ=1 AngleXU=0 Radius=2 StartAngle=2.77438 EndAngle=4.71239
    g3: ArcOfCircle CenterX=7e-16 CenterY=-42.9357 CenterZ=0 NormalX=0 NormalY=0 NormalZ=1 AngleXU=0 Radius=3.75 StartAngle=5.91598 EndAngle=9.79199
  constraints (11):
    c: Tangent(g0,g-3)
    c: Coincident(g1,g0)
    c: Coincident(g1,g-3)
    c: Coincident(g1,g-4)
    c: Coincident(g2,g0)
    c: Coincident(g2,g-5)
    c: Coincident(g2,g-5)
    c: Tangent(g0,g-5)
    c: Coincident(g3,g2)
    c: Coincident(g3,g1)
    c: Coincident(g3,g-4)
FEATURE [PartDesign::Pad] Pad021
  AddSubType = 0
  AutoTaperInnerAngle = true
  BaseFeature = -> Fillet008
  CheckUpToFaceLimits = true
  ClaimChildren = false
  Direction = (1,1,1)
  Fit = 0
  FitJoin = 0
  InnerFit = 0
  InnerFitJoin = 0
  InvalidShape = false
  Length = 1.5
  Length2 = 100
  NewSolid = false
  Profile = -> Sketch034
  Reversed = true
  Suppress = false
  TaperInnerAngle = 0
  TaperInnerAngleRev = 0
  TreeRank = 0
  Type = 0
  ValidateShape = true
  _ProfileBasedVersion = 0
FEATURE [PartDesign::Pocket] Pocket014
  AddSubType = 1
  AutoTaperInnerAngle = true
  BaseFeature = -> Pad021
  CheckUpToFaceLimits = true
  ClaimChildren = false
  Direction = (1,1,1)
  Fit = 0
  FitJoin = 0
  InnerFit = 0
  InnerFitJoin = 0
  InvalidShape = false
  Length = 5
  Length2 = 100
  NewSolid = false
  Profile = -> Sketch035
  Suppress = false
  TaperInnerAngle = 0
  TaperInnerAngleRev = 0
  TreeRank = 0
  Type = 1
  ValidateShape = true
  _ProfileBasedVersion = 0
  _Version = 0
FEATURE [Sketcher::SketchObject] Sketch036
  ArcFitTolerance = 0
  AttachmentSupport = -> [Pocket014]
  ExternalBSplineMaxDegree = 0
  ExternalBSplineTolerance = 0
  FullyConstrained = false
  InternalTolerance = 1e-06
  InvalidShape = false
  MakeInternals = false
  MapMode = 5
  Placement = pos=(0,0,0) rot=(0.57735,0.57735,0.57735;2.0944rad)
  Support = -> [Pocket014]
  TreeRank = 0
  ValidateShape = false
  sketch-geometry (1):
    g0: Circle CenterX=87.5 CenterY=-5 CenterZ=0 NormalX=0 NormalY=0 NormalZ=1 AngleXU=0 Radius=2
  constraints (3):
    c: Diameter(g0) = 4
    c: DistanceY(g0,g-1) = 5
    c: DistanceX(g-1,g0) = 87.5
FEATURE [PartDesign::Pad] Pad022
  AddSubType = 0
  AutoTaperInnerAngle = true
  BaseFeature = -> Pocket014
  CheckUpToFaceLimits = true
  ClaimChildren = false
  Direction = (1,1,1)
  Fit = 0
  FitJoin = 0
  InnerFit = 0
  InnerFitJoin = 0
  InvalidShape = false
  Length = 5
  Length2 = 100
  NewSolid = false
  Profile = -> Sketch036
  Suppress = false
  TaperInnerAngle = 0
  TaperInnerAngleRev = 0
  TreeRank = 0
  Type = 0
  ValidateShape = true
  _ProfileBasedVersion = 0
FEATURE [Sketcher::SketchObject] Sketch037
  ArcFitTolerance = 0
  AttachmentSupport = -> [Pad022]
  ExternalBSplineMaxDegree = 0
  ExternalBSplineTolerance = 0
  FullyConstrained = false
  InternalTolerance = 1e-06
  InvalidShape = false
  MakeInternals = false
  MapMode = 5
  Placement = pos=(0,0,0) rot=(0.57735,0.57735,0.57735;2.0944rad)
  Support = -> [Pad022]
  TreeRank = 0
  ValidateShape = false
  sketch-geometry (1):
    g0: Circle CenterX=-87.5 CenterY=-5 CenterZ=0 NormalX=0 NormalY=0 NormalZ=1 AngleXU=0 Radius=2.5
  constraints (3):
    c: Diameter(g0) = 5
    c: DistanceY(g0,g-1) = 5
    c: DistanceX(g0,g-1) = 87.5
FEATURE [PartDesign::Pocket] Pocket015
  AddSubType = 1
  AutoTaperInnerAngle = true
  BaseFeature = -> Pad022
  CheckUpToFaceLimits = true
  ClaimChildren = false
  Direction = (1,1,1)
  Fit = 0
  FitJoin = 0
  InnerFit = 0
  InnerFitJoin = 0
  InvalidShape = false
  Length = 5.5
  Length2 = 100
  NewSolid = false
  Profile = -> Sketch037
  Suppress = false
  TaperInnerAngle = 0
  TaperInnerAngleRev = 0
  TreeRank = 0
  Type = 0
  ValidateShape = true
  _ProfileBasedVersion = 0
  _Version = 0
FEATURE [PartDesign::Chamfer] Chamfer007
  AddSubType = 0
  Angle = 45
  Base = -> Pocket015 [Edge116,Edge56]
  BaseFeature = -> Pocket015
  ChamferType = 0
  FlipDirection = false
  InvalidShape = false
  NewSolid = false
  Size = 1
  Size2 = 1
  SupportTransform = true
  Suppress = false
  TreeRank = 0
  UseAllEdges = false
  ValidateShape = true
FEATURE [Sketcher::SketchObject] Sketch038
  ArcFitTolerance = 0
  AttachmentSupport = -> [Chamfer007]
  ExternalBSplineMaxDegree = 0
  ExternalBSplineTolerance = 0
  FullyConstrained = false
  InternalTolerance = 1e-06
  InvalidShape = false
  MakeInternals = false
  MapMode = 5
  Placement = pos=(0,0,0) rot=(0.57735,0.57735,0.57735;2.0944rad)
  Support = -> [Chamfer007]
  TreeRank = 0
  ValidateShape = false
  sketch-geometry (4):
    g0: Circle CenterX=87.5 CenterY=-16.69 CenterZ=0 NormalX=0 NormalY=0 NormalZ=1 AngleXU=0 Radius=1.65
    g1: Circle CenterX=87.5 CenterY=-31.69 CenterZ=0 NormalX=0 NormalY=0 NormalZ=1 AngleXU=0 Radius=1.65
    g2: Circle CenterX=-87.5 CenterY=-16.69 CenterZ=0 NormalX=0 NormalY=0 NormalZ=1 AngleXU=0 Radius=1.65
    g3: Circle CenterX=-87.5 CenterY=-31.69 CenterZ=0 NormalX=0 NormalY=0 NormalZ=1 AngleXU=0 Radius=1.65
  constraints (10):
    c: DistanceY(g0,g-1) = 16.69
    c: DistanceY(g1,g-1) = 31.69
    c: DistanceX(g-1,g0) = 87.5
    c: Symmetric(g0,g2,g-2)
    c: Symmetric(g3,g1,g-2)
    c: Vertical(g1,g0)
    c: Equal(g0,g1)
    c: Equal(g1,g2)
    c: Equal(g2,g3)
    c: Diameter(g0) = 3.3
FEATURE [PartDesign::Pocket] Pocket016
  AddSubType = 1
  AutoTaperInnerAngle = true
  BaseFeature = -> Chamfer007
  CheckUpToFaceLimits = true
  ClaimChildren = false
  Direction = (1,1,1)
  Fit = 0
  FitJoin = 0
  InnerFit = 0
  InnerFitJoin = 0
  InvalidShape = false
  Length = 5
  Length2 = 100
  NewSolid = false
  Profile = -> Sketch038
  Suppress = false
  TaperInnerAngle = 0
  TaperInnerAngleRev = 0
  TreeRank = 0
  Type = 1
  ValidateShape = true
  _ProfileBasedVersion = 0
  _Version = 0
FEATURE [Sketcher::SketchObject] Sketch039
  ArcFitTolerance = 0
  AttachmentSupport = -> [Pocket016]
  ExternalBSplineMaxDegree = 0
  ExternalBSplineTolerance = 0
  FullyConstrained = false
  InternalTolerance = 1e-06
  InvalidShape = false
  MakeInternals = false
  MapMode = 5
  Placement = pos=(-7.36667,0,-1e-16) rot=(0.57735,-0.57735,-0.57735;2.0944rad)
  Support = -> [Pocket016]
  TreeRank = 0
  ValidateShape = false
  sketch-geometry (2):
    g0: Circle CenterX=-87.5 CenterY=-31.69 CenterZ=0 NormalX=0 NormalY=0 NormalZ=1 AngleXU=0 Radius=2
    g1: Circle CenterX=-87.5 CenterY=-16.69 CenterZ=0 NormalX=0 NormalY=0 NormalZ=1 AngleXU=0 Radius=2
  constraints (6):
    c: Equal(g1,g0)
    c: Diameter(g0) = 4
    c: DistanceY(g1,g-1) = 16.69
    c: DistanceY(g0,g-1) = 31.69
    c: DistanceX(g1,g-1) = 87.5
    c: Vertical(g1,g0)
FEATURE [PartDesign::Pocket] Pocket017
  AddSubType = 1
  AutoTaperInnerAngle = true
  BaseFeature = -> Pocket016
  CheckUpToFaceLimits = true
  ClaimChildren = false
  Direction = (1,1,1)
  Fit = 0
  FitJoin = 0
  InnerFit = 0
  InnerFitJoin = 0
  InvalidShape = false
  Length = 6
  Length2 = 100
  NewSolid = false
  Profile = -> Sketch039
  Suppress = false
  TaperInnerAngle = 0
  TaperInnerAngleRev = 0
  TreeRank = 0
  Type = 0
  ValidateShape = true
  _ProfileBasedVersion = 0
  _Version = 0
FEATURE [PartDesign::Pocket] Pocket018
  AddSubType = 1
  AutoTaperInnerAngle = true
  BaseFeature = -> Pocket017
  CheckUpToFaceLimits = true
  ClaimChildren = false
  Direction = (1,1,1)
  Fit = 0
  FitJoin = 0
  InnerFit = 0
  InnerFitJoin = 0
  InvalidShape = false
  Length = 5
  Length2 = 100
  NewSolid = false
  Profile = -> Sketch039
  Reversed = true
  Suppress = false
  TaperInnerAngle = 0
  TaperInnerAngleRev = 0
  TreeRank = 0
  Type = 1
  ValidateShape = true
  _ProfileBasedVersion = 0
  _Version = 0
FEATURE [Sketcher::SketchObject] Sketch040
  ArcFitTolerance = 0
  AttachmentSupport = -> [Pocket018]
  ExternalBSplineMaxDegree = 0
  ExternalBSplineTolerance = 0
  FullyConstrained = false
  InternalTolerance = 1e-06
  InvalidShape = false
  MakeInternals = false
  MapMode = 5
  Placement = pos=(-7.36667,0,-1e-16) rot=(0.57735,-0.57735,-0.57735;2.0944rad)
  Support = -> [Pocket018]
  TreeRank = 0
  ValidateShape = false
  sketch-geometry (2):
    g0: Circle CenterX=87.5 CenterY=-16.69 CenterZ=0 NormalX=0 NormalY=0 NormalZ=1 AngleXU=0 Radius=3
    g1: Circle CenterX=87.5 CenterY=-31.69 CenterZ=0 NormalX=0 NormalY=0 NormalZ=1 AngleXU=0 Radius=3
  constraints (6):
    c: Equal(g0,g1)
    c: Diameter(g0) = 6
    c: DistanceY(g1,g-1) = 31.69
    c: DistanceY(g0,g-1) = 16.69
    c: DistanceX(g-1,g0) = 87.5
    c: Vertical(g0,g1)
FEATURE [PartDesign::Pocket] Pocket019
  AddSubType = 1
  AutoTaperInnerAngle = true
  BaseFeature = -> Pocket018
  CheckUpToFaceLimits = true
  ClaimChildren = false
  Direction = (1,1,1)
  Fit = 0
  FitJoin = 0
  InnerFit = 0
  InnerFitJoin = 0
  InvalidShape = false
  Length = 3
  Length2 = 100
  NewSolid = false
  Profile = -> Sketch040
  Suppress = false
  TaperInnerAngle = 0
  TaperInnerAngleRev = 0
  TreeRank = 0
  Type = 0
  ValidateShape = true
  _ProfileBasedVersion = 0
  _Version = 0
FEATURE [PartDesign::Pocket] Pocket020
  AddSubType = 1
  AutoTaperInnerAngle = true
  BaseFeature = -> Pocket019
  CheckUpToFaceLimits = true
  ClaimChildren = false
  Direction = (1,1,1)
  Fit = 0
  FitJoin = 0
  InnerFit = 0
  InnerFitJoin = 0
  InvalidShape = false
  Length = 5
  Length2 = 100
  NewSolid = false
  Profile = -> Sketch040
  Reversed = true
  Suppress = false
  TaperInnerAngle = 0
  TaperInnerAngleRev = 0
  TreeRank = 0
  Type = 1
  ValidateShape = true
  _ProfileBasedVersion = 0
  _Version = 0
FEATURE [PartDesign::Pocket] Pocket021
  AddSubType = 1
  AutoTaperInnerAngle = true
  BaseFeature = -> Pocket020
  CheckUpToFaceLimits = true
  ClaimChildren = false
  Direction = (1,1,1)
  Fit = 0
  FitJoin = 0
  InnerFit = 0
  InnerFitJoin = 0
  InvalidShape = false
  Length = 5
  Length2 = 100
  Midplane = true
  NewSolid = false
  Profile = -> Pocket020 [Face41]
  Suppress = false
  TaperInnerAngle = 0
  TaperInnerAngleRev = 0
  TreeRank = 0
  Type = 1
  ValidateShape = true
  _ProfileBasedVersion = 0
  _Version = 0
FEATURE [PartDesign::Body] Body004
  AutoGroupSolids = false
  ClaimAllChildren = false
  ExportMode = 0
  Group = -> [Sketch031,Pad018,Pad019,Sketch033,Pad020,Mirrored004,Fillet008,Sketch034,Pad021,Sketch035,Pocket014,Sketch036,Pad022,Sketch037,Pocket015,Chamfer007,Sketch038,Pocket016,Sketch039,Pocket017,Pocket018,Sketch040,Pocket019,Pocket020,Pocket021]
  InvalidShape = false
  Origin = -> Origin004
  SingleSolid = true
  Tip = -> Pocket021
  TreeRank = 0
  ValidateShape = false
  _ExportChildren = -> [Pad018,Pad019,Pad020,Mirrored004,Fillet008,Pad021,Pocket014,Pad022,Pocket015,Chamfer007,Pocket016,Pocket017,Pocket018,Pocket019,Pocket020,Pocket021]
  _GroupVersion = 1
COMPONENT P5 — recipe-attached ("Body005", modeled in this document).
Construction recipe (the document's own serialized feature program — sketch geometry with constraints, then the solid features built on it; lengths are millimeters unless a unit is written):

FEATURE [Sketcher::SketchObject] Sketch043
  ArcFitTolerance = 0
  AttachmentSupport = -> [XY_Plane005]
  ExternalBSplineMaxDegree = 0
  ExternalBSplineTolerance = 0
  FullyConstrained = false
  InternalTolerance = 1e-06
  InvalidShape = false
  MakeInternals = false
  MapMode = 5
  Support = -> [XY_Plane005]
  TreeRank = 0
  ValidateShape = false
  sketch-geometry (10):
    g0: LineSegment [constr] StartX=0 StartY=0 StartZ=0 EndX=2 EndY=0 EndZ=0
    g1: LineSegment StartX=2 StartY=0 StartZ=0 EndX=2 EndY=6 EndZ=0
    g2: LineSegment StartX=2 StartY=6 StartZ=0 EndX=0 EndY=6 EndZ=0
    g3: LineSegment StartX=0 StartY=6 StartZ=0 EndX=0 EndY=78 EndZ=0
    g4: LineSegment StartX=0 StartY=78 StartZ=0 EndX=3 EndY=78 EndZ=0
    g5: LineSegment StartX=3 StartY=78 StartZ=0 EndX=3 EndY=27.5 EndZ=0
    g6: LineSegment StartX=3 StartY=27.5 StartZ=0 EndX=12.5 EndY=20 EndZ=0
    g7: LineSegment StartX=12.5 StartY=20 StartZ=0 EndX=12.5 EndY=0 EndZ=0
    g8: LineSegment StartX=12.5 StartY=0 StartZ=0 EndX=2 EndY=0 EndZ=0
    g9: GeomPoint [constr] X=-12.5 Y=0 Z=0
  constraints (27):
    c: Coincident(g0,g-1)
    c: PointOnObject(g0,g-1)
    c: Coincident(g1,g0)
    c: Vertical(g1)
    c: Coincident(g1,g2)
    c: PointOnObject(g2,g-2)
    c: Horizontal(g2)
    c: Coincident(g2,g3)
    c: PointOnObject(g3,g-2)
    c: Coincident(g4,g3)
    c: Horizontal(g4)
    c: Coincident(g4,g5)
    c: Vertical(g5)
    c: Coincident(g5,g6)
    c: Coincident(g6,g7)
    c: PointOnObject(g7,g-1)
    c: Vertical(g7)
    c: Coincident(g7,g8)
    c: Coincident(g8,g0)
    c: DistanceY(g1,g1) = 6
    c: DistanceX(g2,g2) = 2
    c: DistanceX(g4,g4) = 3
    c: DistanceY(g-1,g3) = 78
    c: DistanceY(g7,g7) = 20
    c: DistanceY(g6,g5) = 7.5
    c: Symmetric(g9,g7,g-2)
    c: DistanceX(g9,g7) = 25
FEATURE [PartDesign::Revolution] Revolution
  AddSubType = 0
  Angle = 360
  Axis = (0,1,0)
  Base = (0,0,0)
  ClaimChildren = false
  Fit = 0
  FitJoin = 0
  InnerFit = 0
  InnerFitJoin = 0
  InvalidShape = false
  NewSolid = false
  Profile = -> Sketch043
  ReferenceAxis = -> Sketch043 [V_Axis]
  Reversed = true
  Suppress = false
  TreeRank = 0
  ValidateShape = true
  _ProfileBasedVersion = 0
FEATURE [Sketcher::SketchObject] Sketch041
  ArcFitTolerance = 0
  AttachmentSupport = -> [Revolution]
  ExternalBSplineMaxDegree = 0
  ExternalBSplineTolerance = 0
  ExternalGeometry = -> [Revolution]
  FullyConstrained = false
  InternalTolerance = 1e-06
  InvalidShape = false
  MakeInternals = false
  MapMode = 5
  Placement = pos=(0,0,0) rot=(1,0,0;1.5708rad)
  Support = -> [Revolution]
  TreeRank = 0
  ValidateShape = false
  sketch-geometry (1):
    g0: Circle CenterX=0 CenterY=12.5 CenterZ=0 NormalX=0 NormalY=0 NormalZ=1 AngleXU=0 Radius=1.5
  constraints (3):
    c: PointOnObject(g0,g-2)
    c: PointOnObject(g0,g-3)
    c: Diameter(g0) = 3
FEATURE [PartDesign::Pocket] Pocket022
  AddSubType = 1
  AutoTaperInnerAngle = true
  BaseFeature = -> Revolution
  CheckUpToFaceLimits = true
  ClaimChildren = false
  Direction = (1,1,1)
  Fit = 0
  FitJoin = 0
  InnerFit = 0
  InnerFitJoin = 0
  InvalidShape = false
  Length = 5
  Length2 = 100
  NewSolid = false
  Profile = -> Sketch041
  Suppress = false
  TaperInnerAngle = 0
  TaperInnerAngleRev = 0
  TreeRank = 0
  Type = 1
  ValidateShape = true
  _ProfileBasedVersion = 0
  _Version = 0
FEATURE [PartDesign::PolarPattern] PolarPattern
  AddSubType = 0
  Angle = 360
  Axis = -> Sketch041 [N_Axis]
  BaseFeature = -> Pocket022
  CopyShape = true
  InvalidShape = false
  NewSolid = false
  Occurrences = 8
  OriginalSubs = -> [Pocket022]
  Originals = -> [Pocket022]
  ParallelTransform = true
  SubTransform = true
  Suppress = false
  TreeRank = 0
  ValidateShape = true
  _Version = 0
FEATURE [PartDesign::Fillet] Fillet009
  AddSubType = 0
  Base = -> PolarPattern [Face15,Face13,Face11,Face9,Face7,Face5,Face19,Face17]
  BaseFeature = -> PolarPattern
  InvalidShape = false
  NewSolid = false
  Radius = 1.25
  SupportTransform = true
  Suppress = false
  TreeRank = 0
  UseAllEdges = false
  ValidateShape = true
FEATURE [PartDesign::Fillet] Fillet010
  AddSubType = 0
  Base = -> Fillet009 [Edge94]
  BaseFeature = -> Fillet009
  InvalidShape = false
  NewSolid = false
  Radius = 10
  SupportTransform = true
  Suppress = false
  TreeRank = 0
  UseAllEdges = false
  ValidateShape = true
FEATURE [PartDesign::Chamfer] Chamfer008
  AddSubType = 0
  Angle = 45
  Base = -> Fillet010 [Edge144]
  BaseFeature = -> Fillet010
  ChamferType = 0
  FlipDirection = false
  InvalidShape = false
  NewSolid = false
  Size = 0.5
  Size2 = 1
  SupportTransform = true
  Suppress = false
  TreeRank = 0
  UseAllEdges = false
  ValidateShape = true
FEATURE [Sketcher::SketchObject] Sketch042
  ArcFitTolerance = 0
  AttachmentSupport = -> [Chamfer008]
  ExternalBSplineMaxDegree = 0
  ExternalBSplineTolerance = 0
  FullyConstrained = false
  InternalTolerance = 1e-06
  InvalidShape = false
  MakeInternals = false
  MapMode = 5
  Placement = pos=(0,6,0) rot=(1,0,0;1.5708rad)
  Support = -> [Chamfer008]
  TreeRank = 0
  ValidateShape = false
  sketch-geometry (1):
    g0: Circle CenterX=0 CenterY=0 CenterZ=0 NormalX=0 NormalY=0 NormalZ=1 AngleXU=0 Radius=1.5
  constraints (2):
    c: Coincident(g0,g-1)
    c: Diameter(g0) = 3
FEATURE [PartDesign::Pocket] Pocket023
  AddSubType = 1
  AutoTaperInnerAngle = true
  BaseFeature = -> Chamfer008
  CheckUpToFaceLimits = true
  ClaimChildren = false
  Direction = (1,1,1)
  Fit = 0
  FitJoin = 0
  InnerFit = 0
  InnerFitJoin = 0
  InvalidShape = false
  Length = 12
  Length2 = 100
  NewSolid = false
  Profile = -> Sketch042
  Suppress = false
  TaperInnerAngle = 0
  TaperInnerAngleRev = 0
  TreeRank = 0
  Type = 0
  ValidateShape = true
  _ProfileBasedVersion = 0
  _Version = 0
FEATURE [PartDesign::Chamfer] Chamfer009
  AddSubType = 0
  Angle = 45
  Base = -> Pocket023 [Edge153]
  BaseFeature = -> Pocket023
  ChamferType = 0
  FlipDirection = false
  InvalidShape = false
  NewSolid = false
  Size = 0.25
  Size2 = 1
  SupportTransform = true
  Suppress = false
  TreeRank = 0
  UseAllEdges = false
  ValidateShape = true
FEATURE [Part::Part2DObjectPython] InvoluteGear003  # Draft 2D object (typed FeaturePython)
  AddendumCoefficient = 1
  AttachmentSupport = -> [Chamfer009]
  DedendumCoefficient = 1.25
  ExternalGear = true
  HighPrecision = true
  InvalidShape = false
  MapMode = 5
  Modules = 1.3
  NumberOfTeeth = 26
  Placement = pos=(0,78,0) rot=(0,0.707107,0.707107;3.14159rad)
  PressureAngle = 20
  ProfileShiftCoefficient = 0
  RootFilletCoefficient = 0.375
  Support = -> [Chamfer009]
  TreeRank = 0
  ValidateShape = false
FEATURE [PartDesign::Pad] Pad036
  AddSubType = 0
  AutoTaperInnerAngle = true
  BaseFeature = -> Chamfer009
  CheckUpToFaceLimits = true
  ClaimChildren = false
  Direction = (1,1,1)
  Fit = 0
  FitJoin = 0
  InnerFit = 0
  InnerFitJoin = 0
  InvalidShape = false
  Length = 9
  Length2 = 100
  NewSolid = false
  Profile = -> InvoluteGear003
  Suppress = false
  TaperInnerAngle = 0
  TaperInnerAngleRev = 0
  TreeRank = 0
  Type = 0
  ValidateShape = true
  _ProfileBasedVersion = 0
FEATURE [Sketcher::SketchObject] Sketch079
  ArcFitTolerance = 0
  AttachmentSupport = -> [Pad036]
  ExternalBSplineMaxDegree = 0
  ExternalBSplineTolerance = 0
  FullyConstrained = false
  InternalTolerance = 1e-06
  InvalidShape = false
  MakeInternals = false
  MapMode = 5
  Placement = pos=(0,78,0) rot=(1,0,0;1.5708rad)
  Support = -> [Pad036]
  TreeRank = 0
  ValidateShape = false
  sketch-geometry (2):
    g0: Circle CenterX=0 CenterY=0 CenterZ=0 NormalX=0 NormalY=0 NormalZ=1 AngleXU=0 Radius=7.5
    g1: Circle CenterX=0 CenterY=0 CenterZ=0 NormalX=0 NormalY=0 NormalZ=1 AngleXU=0 Radius=3
  constraints (4):
    c: Coincident(g0,g-1)
    c: Diameter(g0) = 15
    c: Coincident(g1,g0)
    c: Diameter(g1) = 6
FEATURE [PartDesign::Pad] Pad037
  AddSubType = 0
  AutoTaperInnerAngle = true
  BaseFeature = -> Pad036
  CheckUpToFaceLimits = true
  ClaimChildren = false
  Direction = (1,1,1)
  Fit = 0
  FitJoin = 0
  InnerFit = 0
  InnerFitJoin = 0
  InvalidShape = false
  Length = 4.5
  Length2 = 100
  NewSolid = false
  Profile = -> Sketch079
  Suppress = false
  TaperInnerAngle = 0
  TaperInnerAngleRev = 0
  TreeRank = 0
  Type = 0
  ValidateShape = true
  _ProfileBasedVersion = 0
FEATURE [PartDesign::SubShapeBinder] Binder001
  BindCopyOnChange = 0
  BindMode = 0
  ClaimChildren = false
  Context = -> Assembly002 [Parts002.Assembly006.Parts006.Body005.Binder001.]
  EdgeTolerance = 1e-06
  FillStyle = 0
  Fuse = false
  InvalidShape = false
  MakeFace = true
  MergeEdges = true
  OffsetFill = false
  OffsetIntersection = false
  OffsetJoinType = 0
  OffsetOpenResult = false
  Outline = false
  PartialLoad = false
  Refine = true
  Relative = true
  SplitEdges = false
  Support = -> [Plane010]
  TightBound = false
  TreeRank = 0
  ValidateShape = false
  _Version = 3
FEATURE [Sketcher::SketchObject] Sketch080
  ArcFitTolerance = 0
  AttachmentSupport = -> [Binder001]
  ExternalBSplineMaxDegree = 0
  ExternalBSplineTolerance = 0
  FullyConstrained = false
  InternalTolerance = 1e-06
  InvalidShape = false
  MakeInternals = false
  MapMode = 5
  Placement = pos=(0,58.5,0) rot=(0,0.707107,0.707107;3.14159rad)
  Support = -> [Binder001]
  TreeRank = 0
  ValidateShape = false
  sketch-geometry (2):
    g0: Circle CenterX=0 CenterY=0 CenterZ=0 NormalX=0 NormalY=0 NormalZ=1 AngleXU=0 Radius=3
    g1: Circle CenterX=0 CenterY=0 CenterZ=0 NormalX=0 NormalY=0 NormalZ=1 AngleXU=0 Radius=7.5
  constraints (4):
    c: Coincident(g0,g-1)
    c: Coincident(g1,g0)
    c: Diameter(g0) = 6
    c: Diameter(g1) = 15
FEATURE [PartDesign::Pad] Pad038
  AddSubType = 0
  AutoTaperInnerAngle = true
  BaseFeature = -> Pad037
  CheckUpToFaceLimits = true
  ClaimChildren = false
  Direction = (1,1,1)
  Fit = 0
  FitJoin = 0
  InnerFit = 0
  InnerFitJoin = 0
  InvalidShape = false
  Length = 5
  Length2 = 100
  NewSolid = false
  Profile = -> Sketch080
  Reversed = true
  Suppress = false
  TaperInnerAngle = 0
  TaperInnerAngleRev = 0
  TreeRank = 0
  Type = 0
  ValidateShape = true
  _ProfileBasedVersion = 0
FEATURE [PartDesign::Fillet] Fillet020
  AddSubType = 0
  Base = -> Pad038 [Face326]
  BaseFeature = -> Pad038
  InvalidShape = false
  NewSolid = false
  Radius = 0.7
  SupportTransform = true
  Suppress = false
  TreeRank = 0
  UseAllEdges = false
  ValidateShape = true
FEATURE [PartDesign::Fillet] Fillet021
  AddSubType = 0
  Base = -> Fillet020 [Edge269]
  BaseFeature = -> Fillet020
  InvalidShape = false
  NewSolid = false
  Radius = 3
  SupportTransform = true
  Suppress = false
  TreeRank = 0
  UseAllEdges = false
  ValidateShape = true
FEATURE [PartDesign::Chamfer] Chamfer029
  AddSubType = 0
  Angle = 45
  Base = -> Fillet021 [Edge785,Edge1310,Edge1312]
  BaseFeature = -> Fillet021
  ChamferType = 0
  FlipDirection = false
  InvalidShape = false
  NewSolid = false
  Size = 1
  Size2 = 1
  SupportTransform = true
  Suppress = false
  TreeRank = 0
  UseAllEdges = false
  ValidateShape = true
FEATURE [PartDesign::Body] Body005
  AutoGroupSolids = false
  ClaimAllChildren = false
  ExportMode = 0
  Group = -> [Sketch043,Revolution,Sketch041,Pocket022,PolarPattern,Fillet009,Fillet010,Chamfer008,Sketch042,Pocket023,Chamfer009,InvoluteGear003,Pad036,Sketch079,Pad037,Binder001,Sketch080,Pad038,Fillet020,Fillet021,Chamfer029]
  InvalidShape = false
  Origin = -> Origin005
  SingleSolid = true
  Tip = -> Chamfer029
  TreeRank = 0
  ValidateShape = false
  _ExportChildren = -> [Revolution,Pocket022,PolarPattern,Fillet009,Fillet010,Chamfer008,Pocket023,Chamfer009,Pad036,Pad037,Binder001,Pad038,Fillet020,Fillet021,Chamfer029]
  _GroupVersion = 1
COMPONENT P6 — recipe-attached ("Body006", modeled in this document).
Construction recipe (the document's own serialized feature program — sketch geometry with constraints, then the solid features built on it; lengths are millimeters unless a unit is written):

FEATURE [Sketcher::SketchObject] Sketch044
  ArcFitTolerance = 0
  AttachmentSupport = -> [XY_Plane006]
  ExternalBSplineMaxDegree = 0
  ExternalBSplineTolerance = 0
  FullyConstrained = false
  InternalTolerance = 1e-06
  InvalidShape = false
  MakeInternals = false
  MapMode = 5
  Support = -> [XY_Plane006]
  TreeRank = 0
  ValidateShape = false
  sketch-geometry (2):
    g0: Circle CenterX=0 CenterY=0 CenterZ=0 NormalX=0 NormalY=0 NormalZ=1 AngleXU=0 Radius=150
    g1: Circle CenterX=0 CenterY=0 CenterZ=0 NormalX=0 NormalY=0 NormalZ=1 AngleXU=0 Radius=3.5
  constraints (4):
    c: Coincident(g0,g-1)
    c: Radius(g0) = 150
    c: Coincident(g1,g0)
    c: Diameter(g1) = 7
FEATURE [PartDesign::Pad] Pad023
  AddSubType = 0
  AllowMultiFace = false
  AutoTaperInnerAngle = true
  CheckUpToFaceLimits = true
  ClaimChildren = false
  Direction = (1,1,1)
  Fit = 0
  FitJoin = 0
  InnerFit = 0
  InnerFitJoin = 0
  InvalidShape = false
  Length = 3.5
  Length2 = 100
  Midplane = true
  NewSolid = false
  Profile = -> Sketch044
  Suppress = false
  TaperInnerAngle = 0
  TaperInnerAngleRev = 0
  TreeRank = 0
  Type = 0
  ValidateShape = true
  _ProfileBasedVersion = 0
FEATURE [PartDesign::Fillet] Fillet011
  AddSubType = 0
  Base = -> Pad023 [Face1]
  BaseFeature = -> Pad023
  InvalidShape = false
  NewSolid = false
  Radius = 0.5
  SupportTransform = false
  Suppress = false
  TreeRank = 0
  UseAllEdges = false
  ValidateShape = true
FEATURE [Sketcher::SketchObject] Sketch045
  ArcFitTolerance = 0
  ExternalBSplineMaxDegree = 0
  ExternalBSplineTolerance = 0
  FullyConstrained = false
  InternalTolerance = 1e-06
  InvalidShape = false
  MakeInternals = false
  MapMode = 5
  Placement = pos=(0,0,1.75) rot=(0,0,1;0rad)
  TreeRank = 0
  ValidateShape = false
  sketch-geometry (2):
    g0: Circle CenterX=0 CenterY=0 CenterZ=0 NormalX=0 NormalY=0 NormalZ=1 AngleXU=0 Radius=50
    g1: Circle CenterX=0 CenterY=0 CenterZ=0 NormalX=0 NormalY=0 NormalZ=1 AngleXU=0 Radius=60
  constraints (4):
    c: Coincident(g0,g-1)
    c: Coincident(g1,g0)
    c: Diameter(g0) = 100
    c: Diameter(g1) = 120
FEATURE [PartDesign::Pocket] Pocket024
  AddSubType = 1
  AllowMultiFace = false
  AutoTaperInnerAngle = true
  BaseFeature = -> Fillet011
  CheckUpToFaceLimits = true
  ClaimChildren = false
  Direction = (1,1,1)
  Fit = 0
  FitJoin = 0
  InnerFit = 0
  InnerFitJoin = 0
  InvalidShape = false
  Length = 0.5
  Length2 = 100
  NewSolid = false
  Profile = -> Sketch045
  Suppress = false
  TaperInnerAngle = 0
  TaperInnerAngleRev = 0
  TreeRank = 0
  Type = 0
  ValidateShape = true
  _ProfileBasedVersion = 0
  _Version = 0
FEATURE [PartDesign::Mirrored] Mirrored006
  AddSubType = 0
  BaseFeature = -> Pocket024
  CopyShape = true
  InvalidShape = false
  MirrorPlane = -> XY_Plane006
  NewSolid = false
  OriginalSubs = -> [Pocket024]
  Originals = -> [Pocket024]
  ParallelTransform = true
  SubTransform = true
  Suppress = false
  TreeRank = 0
  ValidateShape = true
  _Version = 0
FEATURE [PartDesign::Body] Body006
  AutoGroupSolids = false
  ClaimAllChildren = false
  ExportMode = 0
  Group = -> [Sketch044,Pad023,Fillet011,Sketch045,Pocket024,Mirrored006]
  InvalidShape = false
  Origin = -> Origin006
  SingleSolid = true
  Tip = -> Mirrored006
  TreeRank = 0
  ValidateShape = false
  _ExportChildren = -> [Pad023,Fillet011,Pocket024,Mirrored006]
  _GroupVersion = 1
COMPONENT P7 — recipe-attached ("Body007", modeled in this document).
Construction recipe (the document's own serialized feature program — sketch geometry with constraints, then the solid features built on it; lengths are millimeters unless a unit is written):

FEATURE [PartDesign::ShapeBinder] CopyMirrored002
  InvalidShape = false
  TraceSupport = false
  TreeRank = 0
  ValidateShape = false
FEATURE [Sketcher::SketchObject] Sketch046
  ArcFitTolerance = 0
  AttachmentSupport = -> [CopyMirrored002]
  ExternalBSplineMaxDegree = 0
  ExternalBSplineTolerance = 0
  FullyConstrained = false
  InternalTolerance = 1e-06
  InvalidShape = false
  MakeInternals = false
  MapMode = 5
  Placement = pos=(0,0,1.75) rot=(0,0,1;0rad)
  Support = -> [CopyMirrored002]
  TreeRank = 0
  ValidateShape = false
  sketch-geometry (2):
    g0: Circle CenterX=0 CenterY=0 CenterZ=0 NormalX=0 NormalY=0 NormalZ=1 AngleXU=0 Radius=62
    g1: Circle [constr] CenterX=0 CenterY=0 CenterZ=0 NormalX=0 NormalY=0 NormalZ=1 AngleXU=0 Radius=52
  constraints (4):
    c: Coincident(g0,g-1)
    c: Radius(g0) = 62
    c: Coincident(g1,g0)
    c: Radius(g1) = 52
FEATURE [PartDesign::Pad] Pad024
  AddSubType = 0
  AllowMultiFace = false
  AutoTaperInnerAngle = true
  CheckUpToFaceLimits = true
  ClaimChildren = false
  Direction = (1,1,1)
  Fit = 0
  FitJoin = 0
  InnerFit = 0
  InnerFitJoin = 0
  InvalidShape = false
  Length = 6
  Length2 = 100
  NewSolid = false
  Profile = -> Sketch046
  Suppress = false
  TaperInnerAngle = 0
  TaperInnerAngleRev = 0
  TreeRank = 0
  Type = 0
  ValidateShape = true
  _ProfileBasedVersion = 0
FEATURE [Sketcher::SketchObject] Sketch047
  ArcFitTolerance = 0
  ExternalBSplineMaxDegree = 0
  ExternalBSplineTolerance = 0
  FullyConstrained = false
  InternalTolerance = 1e-06
  InvalidShape = false
  MakeInternals = false
  MapMode = 5
  Placement = pos=(0,0,-8.25) rot=(1,0,0;3.14159rad)
  TreeRank = 0
  ValidateShape = false
  sketch-geometry (1):
    g0: Circle CenterX=0 CenterY=0 CenterZ=0 NormalX=0 NormalY=0 NormalZ=1 AngleXU=0 Radius=4
  constraints (2):
    c: Coincident(g0,g-1)
    c: Diameter(g0) = 8
FEATURE [PartDesign::Pocket] Pocket026
  AddSubType = 1
  AllowMultiFace = false
  AutoTaperInnerAngle = true
  BaseFeature = -> Pad024
  CheckUpToFaceLimits = true
  ClaimChildren = false
  Direction = (1,1,1)
  Fit = 0
  FitJoin = 0
  InnerFit = 0
  InnerFitJoin = 0
  InvalidShape = false
  Length = 5
  Length2 = 100
  Midplane = true
  NewSolid = false
  Profile = -> Sketch047
  Reversed = true
  Suppress = false
  TaperInnerAngle = 0
  TaperInnerAngleRev = 0
  TreeRank = 0
  Type = 1
  ValidateShape = true
  _ProfileBasedVersion = 0
  _Version = 0
FEATURE [Sketcher::SketchObject] Sketch048
  ArcFitTolerance = 0
  ExternalBSplineMaxDegree = 0
  ExternalBSplineTolerance = 0
  FullyConstrained = false
  InternalTolerance = 1e-06
  InvalidShape = false
  MakeInternals = false
  MapMode = 5
  Placement = pos=(0,0,1.75) rot=(1,0,0;3.14159rad)
  TreeRank = 0
  ValidateShape = false
  sketch-geometry (2):
    g0: Circle CenterX=0 CenterY=0 CenterZ=0 NormalX=0 NormalY=0 NormalZ=1 AngleXU=0 Radius=53.5
    g1: Circle CenterX=0 CenterY=0 CenterZ=0 NormalX=0 NormalY=0 NormalZ=1 AngleXU=0 Radius=56.5
  constraints (4):
    c: Coincident(g0,g-1)
    c: Coincident(g1,g0)
    c: Diameter(g0) = 107
    c: Diameter(g1) = 113
FEATURE [PartDesign::Pocket] Pocket027
  AddSubType = 1
  AllowMultiFace = false
  AutoTaperInnerAngle = true
  BaseFeature = -> Pocket026
  CheckUpToFaceLimits = true
  ClaimChildren = false
  Direction = (1,1,1)
  Fit = 0
  FitJoin = 0
  InnerFit = 0
  InnerFitJoin = 0
  InvalidShape = false
  Length = 3
  Length2 = 100
  NewSolid = false
  Profile = -> Sketch048
  Suppress = false
  TaperInnerAngle = 0
  TaperInnerAngleRev = 0
  TreeRank = 0
  Type = 0
  ValidateShape = true
  _ProfileBasedVersion = 0
  _Version = 0
FEATURE [PartDesign::Draft] Draft003
  AddSubType = 0
  Angle = 5
  Base = -> Pocket027 [Face8]
  BaseFeature = -> Pocket027
  InvalidShape = false
  NeutralPlane = -> Pocket027 [Face3]
  NewSolid = false
  SupportTransform = false
  Suppress = false
  TreeRank = 0
  ValidateShape = true
FEATURE [PartDesign::Draft] Draft004
  AddSubType = 0
  Angle = 5
  Base = -> Draft003 [Face8]
  BaseFeature = -> Draft003
  InvalidShape = false
  NeutralPlane = -> Draft003 [Face7]
  NewSolid = false
  SupportTransform = false
  Suppress = false
  TreeRank = 0
  ValidateShape = true
FEATURE [PartDesign::Chamfer] Chamfer012
  AddSubType = 0
  Angle = 45
  Base = -> Draft004 [Face1]
  BaseFeature = -> Draft004
  ChamferType = 0
  FlipDirection = false
  InvalidShape = false
  NewSolid = false
  Size = 1
  Size2 = 1
  SupportTransform = true
  Suppress = false
  TreeRank = 0
  UseAllEdges = false
  ValidateShape = true
FEATURE [Sketcher::SketchObject] Sketch049
  ArcFitTolerance = 0
  AttachmentSupport = -> [YZ_Plane007]
  ExternalBSplineMaxDegree = 0
  ExternalBSplineTolerance = 0
  ExternalGeometry = -> [Chamfer012]
  FullyConstrained = false
  InternalTolerance = 1e-06
  InvalidShape = false
  MakeInternals = false
  MapMode = 5
  Placement = pos=(0,0,0) rot=(0.57735,0.57735,0.57735;2.0944rad)
  Support = -> [YZ_Plane007]
  TreeRank = 0
  ValidateShape = false
  sketch-geometry (9):
    g0: LineSegment StartX=4 StartY=7.75 StartZ=0 EndX=4 EndY=12.75 EndZ=0
    g1: LineSegment StartX=4 StartY=12.75 StartZ=0 EndX=5 EndY=12.75 EndZ=0
    g2: LineSegment StartX=5 StartY=12.75 StartZ=0 EndX=5 EndY=14.75 EndZ=0
    g3: LineSegment StartX=5 StartY=14.75 StartZ=0 EndX=4 EndY=14.75 EndZ=0
    g4: LineSegment StartX=4 StartY=14.75 StartZ=0 EndX=4 EndY=17.75 EndZ=0
    g5: LineSegment StartX=4 StartY=17.75 StartZ=0 EndX=12.5 EndY=17.75 EndZ=0
    g6: LineSegment StartX=12.5 StartY=17.75 StartZ=0 EndX=12.5 EndY=7.75 EndZ=0
    g7: LineSegment StartX=12.5 StartY=7.75 StartZ=0 EndX=4 EndY=7.75 EndZ=0
    g8: GeomPoint [constr] X=-12.5 Y=7.75 Z=0
  constraints (24):
    c: Vertical(g0)
    c: Coincident(g0,g1)
    c: Horizontal(g1)
    c: Coincident(g1,g2)
    c: Vertical(g2)
    c: Coincident(g2,g3)
    c: Horizontal(g3)
    c: Coincident(g3,g4)
    c: Vertical(g4)
    c: Coincident(g4,g5)
    c: Horizontal(g5)
    c: Coincident(g5,g6)
    c: Vertical(g6)
    c: Coincident(g6,g7)
    c: Coincident(g7,g0)
    c: Horizontal(g7)
    c: DistanceY(g6,g6) = 10
    c: Symmetric(g6,g8,g-2)
    c: DistanceX(g8,g6) = 25
    c: DistanceY(g0,g0) = 5
    c: DistanceY(g2,g2) = 2
    c: DistanceX(g1,g1) = 1
    c: Vertical(g3,g0)
    c: Coincident(g0,g-3)
FEATURE [PartDesign::Revolution] Revolution001
  AddSubType = 0
  Angle = 360
  Axis = (-2e-16,3e-16,1)
  Base = (0,0,0)
  BaseFeature = -> Chamfer012
  ClaimChildren = false
  Fit = 0
  FitJoin = 0
  InnerFit = 0
  InnerFitJoin = 0
  InvalidShape = false
  NewSolid = false
  Profile = -> Sketch049
  ReferenceAxis = -> Sketch049 [V_Axis]
  Reversed = true
  Suppress = false
  TreeRank = 0
  ValidateShape = true
  _ProfileBasedVersion = 0
FEATURE [PartDesign::Fillet] Fillet012
  AddSubType = 0
  Base = -> Revolution001 [Edge9]
  BaseFeature = -> Revolution001
  InvalidShape = false
  NewSolid = false
  Radius = 4
  SupportTransform = true
  Suppress = false
  TreeRank = 0
  UseAllEdges = false
  ValidateShape = true
FEATURE [Sketcher::SketchObject] Sketch050
  ArcFitTolerance = 0
  AttachmentSupport = -> [XZ_Plane007]
  ExternalBSplineMaxDegree = 0
  ExternalBSplineTolerance = 0
  FullyConstrained = false
  InternalTolerance = 1e-06
  InvalidShape = false
  MakeInternals = false
  MapMode = 5
  Placement = pos=(0,0,0) rot=(1,0,0;1.5708rad)
  Support = -> [XZ_Plane007]
  TreeRank = 0
  ValidateShape = false
  sketch-geometry (2):
    g0: Circle CenterX=14.5 CenterY=13 CenterZ=0 NormalX=0 NormalY=0 NormalZ=1 AngleXU=0 Radius=4.5
    g1: Circle CenterX=-14.5 CenterY=13 CenterZ=0 NormalX=0 NormalY=0 NormalZ=1 AngleXU=0 Radius=4.5
  constraints (5):
    c: Equal(g1,g0)
    c: Symmetric(g1,g0,g-2)
    c: DistanceY(g-1,g0) = 13
    c: DistanceX(g-1,g0) = 14.5
    c: Diameter(g0) = 9
FEATURE [PartDesign::Pocket] Pocket025
  AddSubType = 1
  AutoTaperInnerAngle = true
  BaseFeature = -> Fillet012
  CheckUpToFaceLimits = true
  ClaimChildren = false
  Direction = (1,1,1)
  Fit = 0
  FitJoin = 0
  InnerFit = 0
  InnerFitJoin = 0
  InvalidShape = false
  Length = 5
  Length2 = 100
  Midplane = true
  NewSolid = false
  Profile = -> Sketch050
  Suppress = false
  TaperInnerAngle = 0
  TaperInnerAngleRev = 0
  TreeRank = 0
  Type = 1
  ValidateShape = true
  _ProfileBasedVersion = 0
  _Version = 0
FEATURE [PartDesign::Chamfer] Chamfer010
  AddSubType = 0
  Angle = 45
  Base = -> Pocket025 [Face9]
  BaseFeature = -> Pocket025
  ChamferType = 0
  FlipDirection = false
  InvalidShape = false
  NewSolid = false
  Size = 0.5
  Size2 = 1
  SupportTransform = true
  Suppress = false
  TreeRank = 0
  UseAllEdges = false
  ValidateShape = true
FEATURE [PartDesign::Chamfer] Chamfer011
  AddSubType = 0
  Angle = 45
  Base = -> Chamfer010 [Face23,Edge32]
  BaseFeature = -> Chamfer010
  ChamferType = 0
  FlipDirection = false
  InvalidShape = false
  NewSolid = false
  Size = 0.5
  Size2 = 1
  SupportTransform = true
  Suppress = false
  TreeRank = 0
  UseAllEdges = false
  ValidateShape = true
FEATURE [PartDesign::Body] Body007
  AutoGroupSolids = false
  ClaimAllChildren = false
  ExportMode = 0
  Group = -> [CopyMirrored002,Sketch046,Pad024,Sketch047,Pocket026,Sketch048,Pocket027,Draft003,Draft004,Chamfer012,Sketch049,Revolution001,Fillet012,Sketch050,Pocket025,Chamfer010,Chamfer011]
  InvalidShape = false
  Origin = -> Origin007
  SingleSolid = true
  Tip = -> Chamfer011
  TreeRank = 0
  ValidateShape = false
  _ExportChildren = -> [CopyMirrored002,Pad024,Pocket026,Pocket027,Draft003,Draft004,Chamfer012,Revolution001,Fillet012,Pocket025,Chamfer010,Chamfer011]
  _GroupVersion = 1
COMPONENT P8 — recipe-attached ("Body008", modeled in this document).
Construction recipe (the document's own serialized feature program — sketch geometry with constraints, then the solid features built on it; lengths are millimeters unless a unit is written):

FEATURE [Sketcher::SketchObject] Sketch051
  ArcFitTolerance = 0
  AttachmentSupport = -> [XY_Plane008]
  ExternalBSplineMaxDegree = 0
  ExternalBSplineTolerance = 0
  FullyConstrained = false
  InternalTolerance = 1e-06
  InvalidShape = false
  MakeInternals = false
  MapMode = 5
  Support = -> [XY_Plane008]
  TreeRank = 0
  ValidateShape = false
  sketch-geometry (4):
    g0: Circle [constr] CenterX=0 CenterY=0 CenterZ=0 NormalX=0 NormalY=0 NormalZ=1 AngleXU=0 Radius=3
    g1: Circle [constr] CenterX=0 CenterY=0 CenterZ=0 NormalX=0 NormalY=0 NormalZ=1 AngleXU=0 Radius=4
    g2: Circle CenterX=0 CenterY=0 CenterZ=0 NormalX=0 NormalY=0 NormalZ=1 AngleXU=0 Radius=3.125
    g3: Circle CenterX=0 CenterY=0 CenterZ=0 NormalX=0 NormalY=0 NormalZ=1 AngleXU=0 Radius=3.875
  constraints (8):
    c: Coincident(g0,g-1)
    c: Coincident(g1,g0)
    c: Diameter(g0) = 6
    c: Diameter(g1) = 8
    c: Coincident(g2,g-1)
    c: Coincident(g3,g2)
    c: Diameter(g2) = 6.25
    c: Diameter(g3) = 7.75
FEATURE [PartDesign::Pad] Pad025
  AddSubType = 0
  AutoTaperInnerAngle = true
  CheckUpToFaceLimits = true
  ClaimChildren = false
  Direction = (1,1,1)
  Fit = 0
  FitJoin = 0
  InnerFit = 0
  InnerFitJoin = 0
  InvalidShape = false
  Length = 16
  Length2 = 100
  NewSolid = false
  Profile = -> Sketch051
  Suppress = false
  TaperInnerAngle = 0
  TaperInnerAngleRev = 0
  TreeRank = 0
  Type = 0
  ValidateShape = true
  _ProfileBasedVersion = 0
FEATURE [Sketcher::SketchObject] Sketch052
  ArcFitTolerance = 0
  AttachmentSupport = -> [Pad025]
  ExternalBSplineMaxDegree = 0
  ExternalBSplineTolerance = 0
  ExternalGeometry = -> [Pad025]
  FullyConstrained = false
  InternalTolerance = 1e-06
  InvalidShape = false
  MakeInternals = false
  MapMode = 5
  Placement = pos=(0,0,16) rot=(0,0,1;0rad)
  Support = -> [Pad025]
  TreeRank = 0
  ValidateShape = false
  sketch-geometry (2):
    g0: Circle CenterX=0 CenterY=0 CenterZ=0 NormalX=0 NormalY=0 NormalZ=1 AngleXU=0 Radius=3.125
    g1: Circle CenterX=0 CenterY=0 CenterZ=0 NormalX=0 NormalY=0 NormalZ=1 AngleXU=0 Radius=12.5
  constraints (4):
    c: Coincident(g0,g-1)
    c: Coincident(g1,g0)
    c: Diameter(g1) = 25
    c: Equal(g-3,g0)
FEATURE [PartDesign::Pad] Pad026
  AddSubType = 0
  AutoTaperInnerAngle = true
  BaseFeature = -> Pad025
  CheckUpToFaceLimits = true
  ClaimChildren = false
  Direction = (1,1,1)
  Fit = 0
  FitJoin = 0
  InnerFit = 0
  InnerFitJoin = 0
  InvalidShape = false
  Length = 2
  Length2 = 100
  NewSolid = false
  Profile = -> Sketch052
  Suppress = false
  TaperInnerAngle = 0
  TaperInnerAngleRev = 0
  TreeRank = 0
  Type = 0
  ValidateShape = true
  _ProfileBasedVersion = 0
FEATURE [PartDesign::Body] Body008
  AutoGroupSolids = false
  ClaimAllChildren = false
  ExportMode = 0
  Group = -> [Sketch051,Pad025,Sketch052,Pad026]
  InvalidShape = false
  Origin = -> Origin008
  SingleSolid = true
  Tip = -> Pad026
  TreeRank = 0
  ValidateShape = false
  _ExportChildren = -> [Pad025,Pad026]
  _GroupVersion = 1
COMPONENT P9 — recipe-attached ("Body009", modeled in this document).
Construction recipe (the document's own serialized feature program — sketch geometry with constraints, then the solid features built on it; lengths are millimeters unless a unit is written):

FEATURE [Sketcher::SketchObject] Sketch053
  ArcFitTolerance = 0
  ExternalBSplineMaxDegree = 0
  ExternalBSplineTolerance = 0
  FullyConstrained = false
  InternalTolerance = 1e-06
  InvalidShape = false
  MakeInternals = false
  MapMode = 5
  Placement = pos=(0,0,0) rot=(0,0.707107,0.707107;3.14159rad)
  TreeRank = 0
  ValidateShape = false
  sketch-geometry (10):
    g0: LineSegment [constr] StartX=0 StartY=0 StartZ=0 EndX=-55 EndY=0 EndZ=0
    g1: LineSegment [constr] StartX=-55 StartY=0 StartZ=0 EndX=-55 EndY=4.75 EndZ=0
    g2: LineSegment StartX=-52 StartY=0 StartZ=0 EndX=-58 EndY=0 EndZ=0
    g3: LineSegment StartX=-58 StartY=0 StartZ=0 EndX=-58 EndY=1.75 EndZ=0
    g4: LineSegment StartX=-52 StartY=0 StartZ=0 EndX=-52 EndY=1.75 EndZ=0
    g5: LineSegment StartX=-58 StartY=1.75 StartZ=0 EndX=-56 EndY=1.75 EndZ=0
    g6: LineSegment StartX=-52 StartY=1.75 StartZ=0 EndX=-54 EndY=1.75 EndZ=0
    g7: LineSegment StartX=-56 StartY=1.75 StartZ=0 EndX=-56 EndY=4.75 EndZ=0
    g8: LineSegment StartX=-56 StartY=4.75 StartZ=0 EndX=-54 EndY=4.75 EndZ=0
    g9: LineSegment StartX=-54 StartY=4.75 StartZ=0 EndX=-54 EndY=1.75 EndZ=0
  constraints (26):
    c: Coincident(g0,g-1)
    c: PointOnObject(g0,g-1)
    c: DistanceX(g0,g0) = 55
    c: Coincident(g1,g0)
    c: Vertical(g1)
    c: PointOnObject(g2,g0)
    c: Symmetric(g2,g2,g1)
    c: DistanceX(g2,g2) = 6
    c: Coincident(g3,g2)
    c: Coincident(g4,g2)
    c: Symmetric(g3,g4,g1)
    c: Vertical(g4)
    c: DistanceY(g3,g3) = 1.75
    c: Coincident(g5,g3)
    c: Coincident(g6,g4)
    c: Symmetric(g6,g5,g1)
    c: Horizontal(g5)
    c: DistanceX(g5,g5) = 2
    c: Coincident(g7,g5)
    c: Vertical(g7)
    c: Coincident(g8,g7)
    c: Coincident(g9,g8)
    c: Coincident(g9,g6)
    c: Symmetric(g7,g8,g1)
    c: DistanceY(g7,g7) = 3
    c: PointOnObject(g1,g8)
FEATURE [PartDesign::Revolution] Revolution002
  AddSubType = 0
  AllowMultiFace = false
  Angle = 360
  Axis = (-1e-16,2e-16,1)
  Base = (0,0,0)
  ClaimChildren = false
  Fit = 0
  FitJoin = 0
  InnerFit = 0
  InnerFitJoin = 0
  InvalidShape = false
  NewSolid = false
  Placement = pos=(0,0,0) rot=(0,0.707107,0.707107;3.14159rad)
  Profile = -> Sketch053
  ReferenceAxis = -> Sketch053 [V_Axis]
  Suppress = false
  TreeRank = 0
  ValidateShape = true
  _ProfileBasedVersion = 0
FEATURE [PartDesign::Draft] Draft005
  AddSubType = 0
  Angle = 5
  Base = -> Revolution002 [Face4,Face6]
  BaseFeature = -> Revolution002
  InvalidShape = false
  NeutralPlane = -> Revolution002 [Face3]
  NewSolid = false
  Placement = pos=(0,0,0) rot=(0,0.707107,0.707107;3.14159rad)
  Reversed = true
  SupportTransform = false
  Suppress = false
  TreeRank = 0
  ValidateShape = true
FEATURE [PartDesign::Body] Body009
  AutoGroupSolids = false
  ClaimAllChildren = false
  ExportMode = 0
  Group = -> [Sketch053,Revolution002,Draft005]
  InvalidShape = false
  Origin = -> Origin009
  SingleSolid = true
  Tip = -> Draft005
  TreeRank = 0
  ValidateShape = false
  _ExportChildren = -> [Revolution002,Draft005]
  _GroupVersion = 1
COMPONENT P10 — recipe-attached ("Body010", modeled in this document).
Construction recipe (the document's own serialized feature program — sketch geometry with constraints, then the solid features built on it; lengths are millimeters unless a unit is written):

FEATURE [Sketcher::SketchObject] Sketch054
  ArcFitTolerance = 0
  ExternalBSplineMaxDegree = 0
  ExternalBSplineTolerance = 0
  FullyConstrained = false
  InternalTolerance = 1e-06
  InvalidShape = false
  MakeInternals = false
  MapMode = 5
  Placement = pos=(0,0,0) rot=(0,0.707107,0.707107;3.14159rad)
  TreeRank = 0
  ValidateShape = false
  sketch-geometry (10):
    g0: LineSegment [constr] StartX=0 StartY=0 StartZ=0 EndX=-55 EndY=0 EndZ=0
    g1: LineSegment [constr] StartX=-55 StartY=0 StartZ=0 EndX=-55 EndY=4.75 EndZ=0
    g2: LineSegment StartX=-52 StartY=0 StartZ=0 EndX=-58 EndY=0 EndZ=0
    g3: LineSegment StartX=-58 StartY=0 StartZ=0 EndX=-58 EndY=1.75 EndZ=0
    g4: LineSegment StartX=-52 StartY=0 StartZ=0 EndX=-52 EndY=1.75 EndZ=0
    g5: LineSegment StartX=-58 StartY=1.75 StartZ=0 EndX=-56 EndY=1.75 EndZ=0
    g6: LineSegment StartX=-52 StartY=1.75 StartZ=0 EndX=-54 EndY=1.75 EndZ=0
    g7: LineSegment StartX=-56 StartY=1.75 StartZ=0 EndX=-56 EndY=4.75 EndZ=0
    g8: LineSegment StartX=-56 StartY=4.75 StartZ=0 EndX=-54 EndY=4.75 EndZ=0
    g9: LineSegment StartX=-54 StartY=4.75 StartZ=0 EndX=-54 EndY=1.75 EndZ=0
  constraints (26):
    c: Coincident(g0,g-1)
    c: PointOnObject(g0,g-1)
    c: DistanceX(g0,g0) = 55
    c: Coincident(g1,g0)
    c: Vertical(g1)
    c: PointOnObject(g2,g0)
    c: Symmetric(g2,g2,g1)
    c: DistanceX(g2,g2) = 6
    c: Coincident(g3,g2)
    c: Coincident(g4,g2)
    c: Symmetric(g3,g4,g1)
    c: Vertical(g4)
    c: DistanceY(g3,g3) = 1.75
    c: Coincident(g5,g3)
    c: Coincident(g6,g4)
    c: Symmetric(g6,g5,g1)
    c: Horizontal(g5)
    c: DistanceX(g5,g5) = 2
    c: Coincident(g7,g5)
    c: Vertical(g7)
    c: Coincident(g8,g7)
    c: Coincident(g9,g8)
    c: Coincident(g9,g6)
    c: Symmetric(g7,g8,g1)
    c: DistanceY(g7,g7) = 3
    c: PointOnObject(g1,g8)
FEATURE [PartDesign::Revolution] Revolution003
  AddSubType = 0
  AllowMultiFace = false
  Angle = 360
  Axis = (-1e-16,2e-16,1)
  Base = (0,0,0)
  ClaimChildren = false
  Fit = 0
  FitJoin = 0
  InnerFit = 0
  InnerFitJoin = 0
  InvalidShape = false
  NewSolid = false
  Placement = pos=(0,0,0) rot=(0,0.707107,0.707107;3.14159rad)
  Profile = -> Sketch054
  ReferenceAxis = -> Sketch054 [V_Axis]
  Suppress = false
  TreeRank = 0
  ValidateShape = true
  _ProfileBasedVersion = 0
FEATURE [PartDesign::Draft] Draft006
  AddSubType = 0
  Angle = 5
  Base = -> Revolution003 [Face4,Face6]
  BaseFeature = -> Revolution003
  InvalidShape = false
  NeutralPlane = -> Revolution003 [Face3]
  NewSolid = false
  Placement = pos=(0,0,0) rot=(0,0.707107,0.707107;3.14159rad)
  Reversed = true
  SupportTransform = false
  Suppress = false
  TreeRank = 0
  ValidateShape = true
FEATURE [PartDesign::Body] Body010
  AutoGroupSolids = false
  ClaimAllChildren = false
  ExportMode = 0
  Group = -> [Sketch054,Revolution003,Draft006]
  InvalidShape = false
  Origin = -> Origin010
  SingleSolid = true
  Tip = -> Draft006
  TreeRank = 0
  ValidateShape = false
  _ExportChildren = -> [Revolution003,Draft006]
  _GroupVersion = 1
